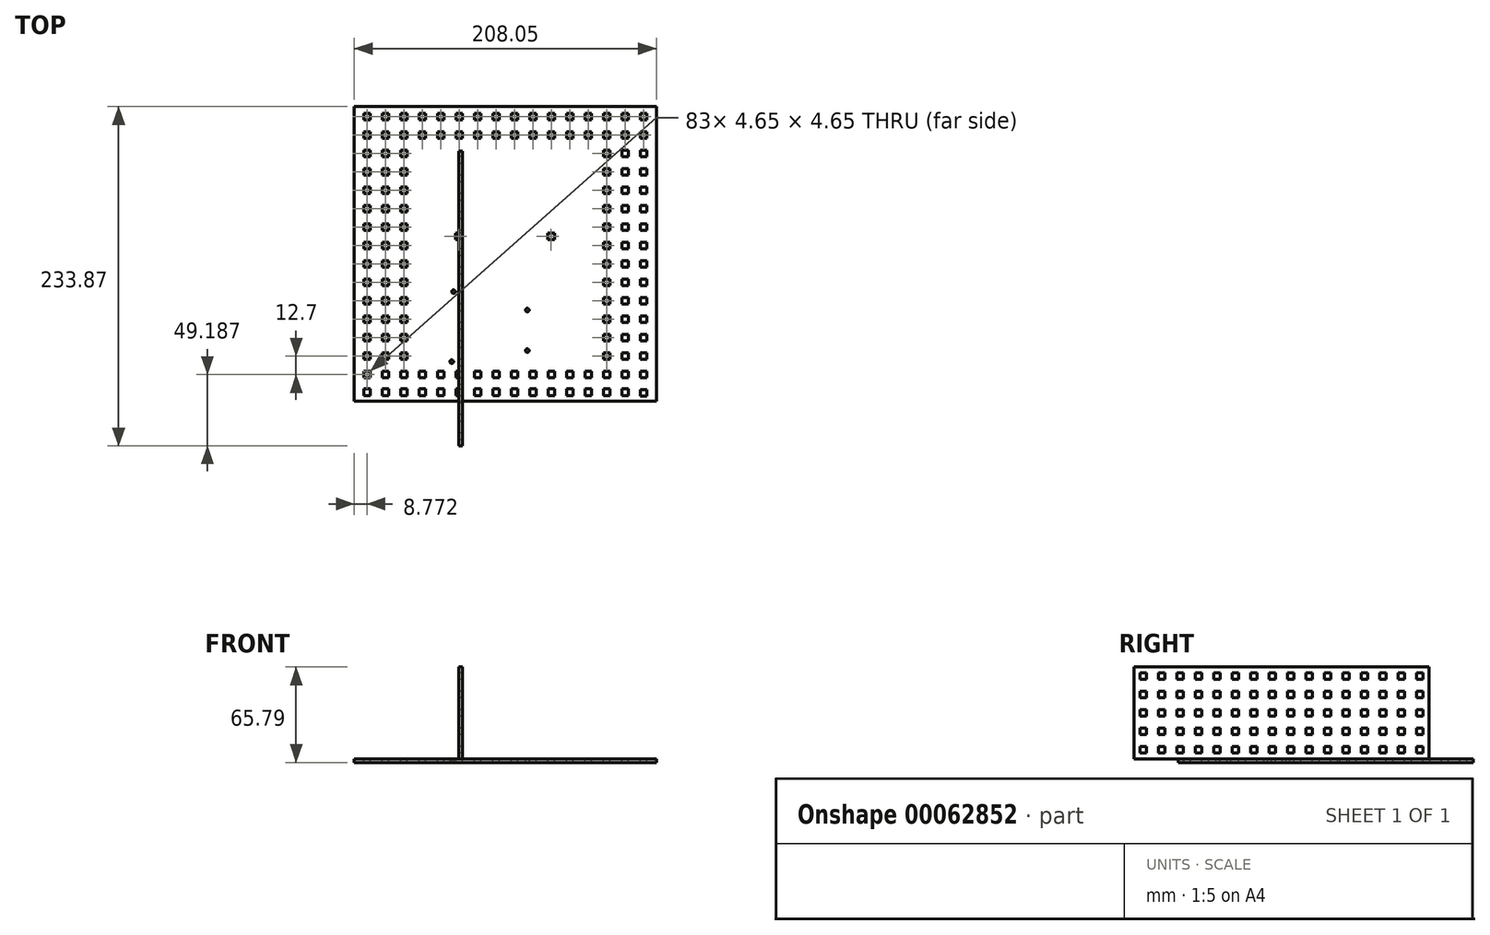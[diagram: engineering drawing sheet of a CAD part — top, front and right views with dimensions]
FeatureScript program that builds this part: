
annotation { "Feature Type Name" : "Feature", "Feature Type Description" : "" }
export const myFeature = defineFeature(function(context is Context, id is Id, definition is map)
    precondition{}
    {
        {
            var Q0;
            Q0=qCreatedBy(makeId("Top.planeOp"),FACE);
            var sketch = newSketch(context, id + "F0", { "sketchPlane" : qUnion([Q0])});
            skLineSegment(sketch, "E0.bottom", {"start": v(129.56, 111.67) * mm, "end": v(124.9, 111.67) * mm});
            skLineSegment(sketch, "E0.top", {"start": v(129.56, 107.05) * mm, "end": v(124.9, 107.05) * mm});
            skLineSegment(sketch, "E0.left", {"start": v(129.56, 111.67) * mm, "end": v(129.56, 107.05) * mm});
            skLineSegment(sketch, "E0.right", {"start": v(124.9, 111.67) * mm, "end": v(124.9, 107.05) * mm});
            skLineSegment(sketch, "E1.0.1.0", {"start": v(129.56, 94.35) * mm, "end": v(124.93, 94.35) * mm});
            skLineSegment(sketch, "E1.0.1.1", {"start": v(129.56, 98.97) * mm, "end": v(129.56, 94.35) * mm});
            skLineSegment(sketch, "E1.0.1.2", {"start": v(124.93, 98.97) * mm, "end": v(124.93, 94.35) * mm});
            skLineSegment(sketch, "E1.0.1.3", {"start": v(129.56, 98.97) * mm, "end": v(124.93, 98.97) * mm});
            skLineSegment(sketch, "E1.0.2.0", {"start": v(129.56, 81.65) * mm, "end": v(124.93, 81.65) * mm});
            skLineSegment(sketch, "E1.0.2.1", {"start": v(129.56, 86.27) * mm, "end": v(129.56, 81.65) * mm});
            skLineSegment(sketch, "E1.0.2.2", {"start": v(124.93, 86.27) * mm, "end": v(124.93, 81.65) * mm});
            skLineSegment(sketch, "E1.0.2.3", {"start": v(129.56, 86.27) * mm, "end": v(124.93, 86.27) * mm});
            skLineSegment(sketch, "E1.0.3.0", {"start": v(129.56, 68.95) * mm, "end": v(124.93, 68.95) * mm});
            skLineSegment(sketch, "E1.0.3.1", {"start": v(129.56, 73.57) * mm, "end": v(129.56, 68.95) * mm});
            skLineSegment(sketch, "E1.0.3.2", {"start": v(124.93, 73.57) * mm, "end": v(124.93, 68.95) * mm});
            skLineSegment(sketch, "E1.0.3.3", {"start": v(129.56, 73.57) * mm, "end": v(124.93, 73.57) * mm});
            skLineSegment(sketch, "E1.0.4.0", {"start": v(129.56, 56.25) * mm, "end": v(124.93, 56.25) * mm});
            skLineSegment(sketch, "E1.0.4.1", {"start": v(129.56, 60.87) * mm, "end": v(129.56, 56.25) * mm});
            skLineSegment(sketch, "E1.0.4.2", {"start": v(124.93, 60.87) * mm, "end": v(124.93, 56.25) * mm});
            skLineSegment(sketch, "E1.0.4.3", {"start": v(129.56, 60.87) * mm, "end": v(124.93, 60.87) * mm});
            skLineSegment(sketch, "E1.0.5.0", {"start": v(129.56, 43.55) * mm, "end": v(124.93, 43.55) * mm});
            skLineSegment(sketch, "E1.0.5.1", {"start": v(129.56, 48.17) * mm, "end": v(129.56, 43.55) * mm});
            skLineSegment(sketch, "E1.0.5.2", {"start": v(124.93, 48.17) * mm, "end": v(124.93, 43.55) * mm});
            skLineSegment(sketch, "E1.0.5.3", {"start": v(129.56, 48.17) * mm, "end": v(124.93, 48.17) * mm});
            skLineSegment(sketch, "E1.0.6.0", {"start": v(129.56, 30.85) * mm, "end": v(124.93, 30.85) * mm});
            skLineSegment(sketch, "E1.0.6.1", {"start": v(129.56, 35.47) * mm, "end": v(129.56, 30.85) * mm});
            skLineSegment(sketch, "E1.0.6.2", {"start": v(124.93, 35.47) * mm, "end": v(124.93, 30.85) * mm});
            skLineSegment(sketch, "E1.0.6.3", {"start": v(129.56, 35.47) * mm, "end": v(124.93, 35.47) * mm});
            skLineSegment(sketch, "E1.0.7.0", {"start": v(129.56, 18.15) * mm, "end": v(124.93, 18.15) * mm});
            skLineSegment(sketch, "E1.0.7.1", {"start": v(129.56, 22.77) * mm, "end": v(129.56, 18.15) * mm});
            skLineSegment(sketch, "E1.0.7.2", {"start": v(124.93, 22.77) * mm, "end": v(124.93, 18.15) * mm});
            skLineSegment(sketch, "E1.0.7.3", {"start": v(129.56, 22.77) * mm, "end": v(124.93, 22.77) * mm});
            skLineSegment(sketch, "E1.0.8.0", {"start": v(129.56, 5.45) * mm, "end": v(124.93, 5.45) * mm});
            skLineSegment(sketch, "E1.0.8.1", {"start": v(129.56, 10.07) * mm, "end": v(129.56, 5.45) * mm});
            skLineSegment(sketch, "E1.0.8.2", {"start": v(124.93, 10.07) * mm, "end": v(124.93, 5.45) * mm});
            skLineSegment(sketch, "E1.0.8.3", {"start": v(129.56, 10.07) * mm, "end": v(124.93, 10.07) * mm});
            skLineSegment(sketch, "E1.0.9.0", {"start": v(129.56, -7.25) * mm, "end": v(124.93, -7.25) * mm});
            skLineSegment(sketch, "E1.0.9.1", {"start": v(129.56, -2.63) * mm, "end": v(129.56, -7.25) * mm});
            skLineSegment(sketch, "E1.0.9.2", {"start": v(124.93, -2.63) * mm, "end": v(124.93, -7.25) * mm});
            skLineSegment(sketch, "E1.0.9.3", {"start": v(129.56, -2.63) * mm, "end": v(124.93, -2.63) * mm});
            skLineSegment(sketch, "E1.0.10.0", {"start": v(129.56, -19.95) * mm, "end": v(124.93, -19.95) * mm});
            skLineSegment(sketch, "E1.0.10.1", {"start": v(129.56, -15.33) * mm, "end": v(129.56, -19.95) * mm});
            skLineSegment(sketch, "E1.0.10.2", {"start": v(124.93, -15.33) * mm, "end": v(124.93, -19.95) * mm});
            skLineSegment(sketch, "E1.0.10.3", {"start": v(129.56, -15.33) * mm, "end": v(124.93, -15.33) * mm});
            skLineSegment(sketch, "E2", {"start": v(-72.04, 141.63) * mm, "end": v(-72.04, -61.57) * mm});
            skLineSegment(sketch, "E3.0.0.12", {"start": v(-60.94, -40.73) * mm, "end": v(-60.94, -45.35) * mm});
            skLineSegment(sketch, "E3.3.0.12", {"start": v(-65.57, -45.35) * mm, "end": v(-60.94, -45.35) * mm});
            skLineSegment(sketch, "E3.6.0.12", {"start": v(-65.57, -40.73) * mm, "end": v(-65.57, -45.35) * mm});
            skLineSegment(sketch, "E3.9.0.12", {"start": v(-65.57, -40.73) * mm, "end": v(-60.94, -40.73) * mm});
            skLineSegment(sketch, "E3.0.0.13", {"start": v(-60.92, -52.9) * mm, "end": v(-60.92, -57.53) * mm});
            skLineSegment(sketch, "E3.3.0.13", {"start": v(-65.57, -57.53) * mm, "end": v(-60.92, -57.53) * mm});
            skLineSegment(sketch, "E3.6.0.13", {"start": v(-65.57, -52.9) * mm, "end": v(-65.57, -57.53) * mm});
            skLineSegment(sketch, "E3.9.0.13", {"start": v(-65.57, -52.9) * mm, "end": v(-60.92, -52.9) * mm});
            skLineSegment(sketch, "E4.0.0.11", {"start": v(129.56, -32.65) * mm, "end": v(124.93, -32.65) * mm});
            skLineSegment(sketch, "E4.3.0.11", {"start": v(129.56, -28.03) * mm, "end": v(129.56, -32.65) * mm});
            skLineSegment(sketch, "E4.6.0.11", {"start": v(124.93, -28.03) * mm, "end": v(124.93, -32.65) * mm});
            skLineSegment(sketch, "E4.9.0.11", {"start": v(129.56, -28.03) * mm, "end": v(124.93, -28.03) * mm});
            skLineSegment(sketch, "E4.0.0.12", {"start": v(129.56, -45.35) * mm, "end": v(124.93, -45.35) * mm});
            skLineSegment(sketch, "E4.3.0.12", {"start": v(129.56, -40.73) * mm, "end": v(129.56, -45.35) * mm});
            skLineSegment(sketch, "E4.6.0.12", {"start": v(124.93, -40.73) * mm, "end": v(124.93, -45.35) * mm});
            skLineSegment(sketch, "E4.9.0.12", {"start": v(129.56, -40.73) * mm, "end": v(124.93, -40.73) * mm});
            skLineSegment(sketch, "E4.0.0.13", {"start": v(129.56, -58.05) * mm, "end": v(124.93, -58.05) * mm});
            skLineSegment(sketch, "E4.3.0.13", {"start": v(129.56, -53.43) * mm, "end": v(129.56, -58.05) * mm});
            skLineSegment(sketch, "E4.6.0.13", {"start": v(124.93, -53.43) * mm, "end": v(124.93, -58.05) * mm});
            skLineSegment(sketch, "E4.9.0.13", {"start": v(129.56, -53.43) * mm, "end": v(124.93, -53.43) * mm});
            skCircle(sketch, "E5", {"center": v(-3.7, 14.1) * mm, "radius": 1.27 * mm});
            skCircle(sketch, "E6", {"center": v(47.1, 1.4) * mm, "radius": 1.27 * mm});
            skCircle(sketch, "E7", {"center": v(47.1, -26.53) * mm, "radius": 1.27 * mm});
            skCircle(sketch, "E8", {"center": v(-4.96, -34.15) * mm, "radius": 1.27 * mm});
            skLineSegment(sketch, "E9", {"start": v(-60.94, 137.07) * mm, "end": v(-60.94, 132.42) * mm});
            skLineSegment(sketch, "E10", {"start": v(-60.94, 132.42) * mm, "end": v(-65.6, 132.42) * mm});
            skLineSegment(sketch, "E11", {"start": v(124.9, 124.37) * mm, "end": v(129.56, 124.37) * mm});
            skLineSegment(sketch, "E12", {"start": v(129.56, 124.37) * mm, "end": v(129.56, 119.72) * mm});
            skLineSegment(sketch, "E13", {"start": v(124.9, 137.07) * mm, "end": v(129.56, 137.07) * mm});
            skLineSegment(sketch, "E14", {"start": v(129.56, 137.07) * mm, "end": v(129.56, 132.42) * mm});
            skLineSegment(sketch, "E15", {"start": v(129.56, 132.42) * mm, "end": v(124.9, 132.42) * mm});
            skLineSegment(sketch, "E16", {"start": v(129.56, 119.72) * mm, "end": v(124.9, 119.72) * mm});
            skLineSegment(sketch, "E17", {"start": v(124.9, 119.72) * mm, "end": v(124.9, 124.37) * mm});
            skLineSegment(sketch, "E18", {"start": v(124.9, 137.07) * mm, "end": v(124.9, 132.42) * mm});
            skLineSegment(sketch, "E19.rect.bottom", {"start": v(2.32, 49.89) * mm, "end": v(-2.32, 49.89) * mm});
            skLineSegment(sketch, "E19.rect.top", {"start": v(2.32, 54.53) * mm, "end": v(-2.32, 54.53) * mm});
            skLineSegment(sketch, "E19.rect.left", {"start": v(2.32, 49.89) * mm, "end": v(2.32, 54.53) * mm});
            skLineSegment(sketch, "E19.rect.right", {"start": v(-2.32, 49.89) * mm, "end": v(-2.32, 54.53) * mm});
            skPoint(sketch, "E19.rect.middle", {"position": v(0, 52.2) * mm});
            skLineSegment(sketch, "E20.rect.bottom", {"start": v(65.82, 49.89) * mm, "end": v(61.18, 49.89) * mm});
            skLineSegment(sketch, "E20.rect.top", {"start": v(65.82, 54.53) * mm, "end": v(61.18, 54.53) * mm});
            skLineSegment(sketch, "E20.rect.left", {"start": v(65.82, 49.89) * mm, "end": v(65.82, 54.53) * mm});
            skLineSegment(sketch, "E20.rect.right", {"start": v(61.18, 49.89) * mm, "end": v(61.18, 54.53) * mm});
            skPoint(sketch, "E20.rect.middle", {"position": v(63.5, 52.2) * mm});
            skLineSegment(sketch, "E21", {"start": v(-72.04, -61.57) * mm, "end": v(136, -61.57) * mm});
            skLineSegment(sketch, "E22", {"start": v(136, 141.63) * mm, "end": v(136, -61.57) * mm});
            skLineSegment(sketch, "E23", {"start": v(-72.04, 141.63) * mm, "end": v(136, 141.63) * mm});
            skLineSegment(sketch, "E24", {"start": v(-60.94, 137.07) * mm, "end": v(-65.6, 137.07) * mm});
            skLineSegment(sketch, "E25", {"start": v(-65.6, 137.07) * mm, "end": v(-65.6, 132.42) * mm});
            skLineSegment(sketch, "E26.1.0.0", {"start": v(-48.24, 137.07) * mm, "end": v(-48.24, 132.42) * mm});
            skLineSegment(sketch, "E26.1.0.1", {"start": v(-48.24, 137.07) * mm, "end": v(-52.9, 137.07) * mm});
            skLineSegment(sketch, "E26.1.0.2", {"start": v(-52.9, 137.07) * mm, "end": v(-52.9, 132.42) * mm});
            skLineSegment(sketch, "E26.1.0.3", {"start": v(-48.24, 132.42) * mm, "end": v(-52.9, 132.42) * mm});
            skLineSegment(sketch, "E26.2.0.0", {"start": v(-35.54, 137.07) * mm, "end": v(-35.54, 132.42) * mm});
            skLineSegment(sketch, "E26.2.0.1", {"start": v(-35.54, 137.07) * mm, "end": v(-40.2, 137.07) * mm});
            skLineSegment(sketch, "E26.2.0.2", {"start": v(-40.2, 137.07) * mm, "end": v(-40.2, 132.42) * mm});
            skLineSegment(sketch, "E26.2.0.3", {"start": v(-35.54, 132.42) * mm, "end": v(-40.2, 132.42) * mm});
            skLineSegment(sketch, "E26.3.0.0", {"start": v(-22.84, 137.07) * mm, "end": v(-22.84, 132.42) * mm});
            skLineSegment(sketch, "E26.3.0.1", {"start": v(-22.84, 137.07) * mm, "end": v(-27.5, 137.07) * mm});
            skLineSegment(sketch, "E26.3.0.2", {"start": v(-27.5, 137.07) * mm, "end": v(-27.5, 132.42) * mm});
            skLineSegment(sketch, "E26.3.0.3", {"start": v(-22.84, 132.42) * mm, "end": v(-27.5, 132.42) * mm});
            skLineSegment(sketch, "E26.4.0.0", {"start": v(-10.14, 137.07) * mm, "end": v(-10.14, 132.42) * mm});
            skLineSegment(sketch, "E26.4.0.1", {"start": v(-10.14, 137.07) * mm, "end": v(-14.8, 137.07) * mm});
            skLineSegment(sketch, "E26.4.0.2", {"start": v(-14.8, 137.07) * mm, "end": v(-14.8, 132.42) * mm});
            skLineSegment(sketch, "E26.4.0.3", {"start": v(-10.14, 132.42) * mm, "end": v(-14.8, 132.42) * mm});
            skLineSegment(sketch, "E26.5.0.0", {"start": v(2.56, 137.07) * mm, "end": v(2.56, 132.42) * mm});
            skLineSegment(sketch, "E26.5.0.1", {"start": v(2.56, 137.07) * mm, "end": v(-2.1, 137.07) * mm});
            skLineSegment(sketch, "E26.5.0.2", {"start": v(-2.1, 137.07) * mm, "end": v(-2.1, 132.42) * mm});
            skLineSegment(sketch, "E26.5.0.3", {"start": v(2.56, 132.42) * mm, "end": v(-2.1, 132.42) * mm});
            skLineSegment(sketch, "E26.6.0.0", {"start": v(15.26, 137.07) * mm, "end": v(15.26, 132.42) * mm});
            skLineSegment(sketch, "E26.6.0.1", {"start": v(15.26, 137.07) * mm, "end": v(10.6, 137.07) * mm});
            skLineSegment(sketch, "E26.6.0.2", {"start": v(10.6, 137.07) * mm, "end": v(10.6, 132.42) * mm});
            skLineSegment(sketch, "E26.6.0.3", {"start": v(15.26, 132.42) * mm, "end": v(10.6, 132.42) * mm});
            skLineSegment(sketch, "E26.7.0.0", {"start": v(27.96, 137.07) * mm, "end": v(27.96, 132.42) * mm});
            skLineSegment(sketch, "E26.7.0.1", {"start": v(27.96, 137.07) * mm, "end": v(23.3, 137.07) * mm});
            skLineSegment(sketch, "E26.7.0.2", {"start": v(23.3, 137.07) * mm, "end": v(23.3, 132.42) * mm});
            skLineSegment(sketch, "E26.7.0.3", {"start": v(27.96, 132.42) * mm, "end": v(23.3, 132.42) * mm});
            skLineSegment(sketch, "E26.8.0.0", {"start": v(40.66, 137.07) * mm, "end": v(40.66, 132.42) * mm});
            skLineSegment(sketch, "E26.8.0.1", {"start": v(40.66, 137.07) * mm, "end": v(36, 137.07) * mm});
            skLineSegment(sketch, "E26.8.0.2", {"start": v(36, 137.07) * mm, "end": v(36, 132.42) * mm});
            skLineSegment(sketch, "E26.8.0.3", {"start": v(40.66, 132.42) * mm, "end": v(36, 132.42) * mm});
            skLineSegment(sketch, "E26.9.0.0", {"start": v(53.36, 137.07) * mm, "end": v(53.36, 132.42) * mm});
            skLineSegment(sketch, "E26.9.0.1", {"start": v(53.36, 137.07) * mm, "end": v(48.7, 137.07) * mm});
            skLineSegment(sketch, "E26.9.0.2", {"start": v(48.7, 137.07) * mm, "end": v(48.7, 132.42) * mm});
            skLineSegment(sketch, "E26.9.0.3", {"start": v(53.36, 132.42) * mm, "end": v(48.7, 132.42) * mm});
            skLineSegment(sketch, "E26.10.0.0", {"start": v(66.06, 137.07) * mm, "end": v(66.06, 132.42) * mm});
            skLineSegment(sketch, "E26.10.0.1", {"start": v(66.06, 137.07) * mm, "end": v(61.4, 137.07) * mm});
            skLineSegment(sketch, "E26.10.0.2", {"start": v(61.4, 137.07) * mm, "end": v(61.4, 132.42) * mm});
            skLineSegment(sketch, "E26.10.0.3", {"start": v(66.06, 132.42) * mm, "end": v(61.4, 132.42) * mm});
            skLineSegment(sketch, "E26.11.0.0", {"start": v(78.76, 137.07) * mm, "end": v(78.76, 132.42) * mm});
            skLineSegment(sketch, "E26.11.0.1", {"start": v(78.76, 137.07) * mm, "end": v(74.1, 137.07) * mm});
            skLineSegment(sketch, "E26.11.0.2", {"start": v(74.1, 137.07) * mm, "end": v(74.1, 132.42) * mm});
            skLineSegment(sketch, "E26.11.0.3", {"start": v(78.76, 132.42) * mm, "end": v(74.1, 132.42) * mm});
            skLineSegment(sketch, "E26.12.0.0", {"start": v(91.46, 137.07) * mm, "end": v(91.46, 132.42) * mm});
            skLineSegment(sketch, "E26.12.0.1", {"start": v(91.46, 137.07) * mm, "end": v(86.8, 137.07) * mm});
            skLineSegment(sketch, "E26.12.0.2", {"start": v(86.8, 137.07) * mm, "end": v(86.8, 132.42) * mm});
            skLineSegment(sketch, "E26.12.0.3", {"start": v(91.46, 132.42) * mm, "end": v(86.8, 132.42) * mm});
            skLineSegment(sketch, "E26.13.0.0", {"start": v(104.16, 137.07) * mm, "end": v(104.16, 132.42) * mm});
            skLineSegment(sketch, "E26.13.0.1", {"start": v(104.16, 137.07) * mm, "end": v(99.5, 137.07) * mm});
            skLineSegment(sketch, "E26.13.0.2", {"start": v(99.5, 137.07) * mm, "end": v(99.5, 132.42) * mm});
            skLineSegment(sketch, "E26.13.0.3", {"start": v(104.16, 132.42) * mm, "end": v(99.5, 132.42) * mm});
            skLineSegment(sketch, "E26.14.0.0", {"start": v(116.86, 137.07) * mm, "end": v(116.86, 132.42) * mm});
            skLineSegment(sketch, "E26.14.0.1", {"start": v(116.86, 137.07) * mm, "end": v(112.2, 137.07) * mm});
            skLineSegment(sketch, "E26.14.0.2", {"start": v(112.2, 137.07) * mm, "end": v(112.2, 132.42) * mm});
            skLineSegment(sketch, "E26.14.0.3", {"start": v(116.86, 132.42) * mm, "end": v(112.2, 132.42) * mm});
            skLineSegment(sketch, "E26.direction1", {"start": v(-60.94, 132.42) * mm, "end": v(-48.24, 132.42) * mm, "construction": true});
            skLineSegment(sketch, "E27", {"start": v(-65.6, 137.07) * mm, "end": v(-72.04, 137.07) * mm});
            skLineSegment(sketch, "E28", {"start": v(-65.6, 124.26) * mm, "end": v(-72.04, 124.26) * mm});
            skLineSegment(sketch, "E29", {"start": v(-65.57, -40.73) * mm, "end": v(-72.04, -40.73) * mm});
            skLineSegment(sketch, "E30", {"start": v(129.56, 124.37) * mm, "end": v(136, 124.37) * mm});
            skLineSegment(sketch, "E31", {"start": v(129.56, 111.67) * mm, "end": v(136, 111.67) * mm});
            skLineSegment(sketch, "E32", {"start": v(129.56, 98.97) * mm, "end": v(136, 98.97) * mm});
            skLineSegment(sketch, "E33", {"start": v(129.56, 86.27) * mm, "end": v(136, 86.27) * mm});
            skLineSegment(sketch, "E34", {"start": v(129.56, 73.57) * mm, "end": v(136, 73.57) * mm});
            skLineSegment(sketch, "E35", {"start": v(129.56, 60.87) * mm, "end": v(136, 60.87) * mm});
            skLineSegment(sketch, "E36", {"start": v(129.56, 48.17) * mm, "end": v(136, 48.17) * mm});
            skLineSegment(sketch, "E37", {"start": v(129.56, 35.47) * mm, "end": v(136, 35.47) * mm});
            skLineSegment(sketch, "E38", {"start": v(129.56, 22.77) * mm, "end": v(136, 22.77) * mm});
            skLineSegment(sketch, "E39", {"start": v(129.56, 10.07) * mm, "end": v(136, 10.07) * mm});
            skLineSegment(sketch, "E40", {"start": v(129.56, -2.63) * mm, "end": v(136, -2.63) * mm});
            skLineSegment(sketch, "E41", {"start": v(129.56, -15.33) * mm, "end": v(136, -15.33) * mm});
            skLineSegment(sketch, "E42", {"start": v(129.56, -28.03) * mm, "end": v(136, -28.03) * mm});
            skLineSegment(sketch, "E43", {"start": v(129.56, -40.73) * mm, "end": v(136, -40.73) * mm});
            skLineSegment(sketch, "E44", {"start": v(129.56, -53.43) * mm, "end": v(136, -53.43) * mm});
            skLineSegment(sketch, "E45.1.0.0", {"start": v(-48.22, -52.9) * mm, "end": v(-48.22, -57.53) * mm});
            skLineSegment(sketch, "E45.1.0.1", {"start": v(-52.87, -52.9) * mm, "end": v(-48.22, -52.9) * mm});
            skLineSegment(sketch, "E45.1.0.2", {"start": v(-52.87, -52.9) * mm, "end": v(-52.87, -57.53) * mm});
            skLineSegment(sketch, "E45.1.0.3", {"start": v(-52.87, -57.53) * mm, "end": v(-48.22, -57.53) * mm});
            skLineSegment(sketch, "E45.2.0.0", {"start": v(-35.52, -52.9) * mm, "end": v(-35.52, -57.53) * mm});
            skLineSegment(sketch, "E45.2.0.1", {"start": v(-40.17, -52.9) * mm, "end": v(-35.52, -52.9) * mm});
            skLineSegment(sketch, "E45.2.0.2", {"start": v(-40.17, -52.9) * mm, "end": v(-40.17, -57.53) * mm});
            skLineSegment(sketch, "E45.2.0.3", {"start": v(-40.17, -57.53) * mm, "end": v(-35.52, -57.53) * mm});
            skLineSegment(sketch, "E45.3.0.0", {"start": v(-22.82, -52.9) * mm, "end": v(-22.82, -57.53) * mm});
            skLineSegment(sketch, "E45.3.0.1", {"start": v(-27.47, -52.9) * mm, "end": v(-22.82, -52.9) * mm});
            skLineSegment(sketch, "E45.3.0.2", {"start": v(-27.47, -52.9) * mm, "end": v(-27.47, -57.53) * mm});
            skLineSegment(sketch, "E45.3.0.3", {"start": v(-27.47, -57.53) * mm, "end": v(-22.82, -57.53) * mm});
            skLineSegment(sketch, "E45.4.0.0", {"start": v(-10.12, -52.9) * mm, "end": v(-10.12, -57.53) * mm});
            skLineSegment(sketch, "E45.4.0.1", {"start": v(-14.77, -52.9) * mm, "end": v(-10.12, -52.9) * mm});
            skLineSegment(sketch, "E45.4.0.2", {"start": v(-14.77, -52.9) * mm, "end": v(-14.77, -57.53) * mm});
            skLineSegment(sketch, "E45.4.0.3", {"start": v(-14.77, -57.53) * mm, "end": v(-10.12, -57.53) * mm});
            skLineSegment(sketch, "E45.5.0.0", {"start": v(2.58, -52.9) * mm, "end": v(2.58, -57.53) * mm});
            skLineSegment(sketch, "E45.5.0.1", {"start": v(-2.07, -52.9) * mm, "end": v(2.58, -52.9) * mm});
            skLineSegment(sketch, "E45.5.0.2", {"start": v(-2.07, -52.9) * mm, "end": v(-2.07, -57.53) * mm});
            skLineSegment(sketch, "E45.5.0.3", {"start": v(-2.07, -57.53) * mm, "end": v(2.58, -57.53) * mm});
            skLineSegment(sketch, "E45.6.0.0", {"start": v(15.28, -52.9) * mm, "end": v(15.28, -57.53) * mm});
            skLineSegment(sketch, "E45.6.0.1", {"start": v(10.63, -52.9) * mm, "end": v(15.28, -52.9) * mm});
            skLineSegment(sketch, "E45.6.0.2", {"start": v(10.63, -52.9) * mm, "end": v(10.63, -57.53) * mm});
            skLineSegment(sketch, "E45.6.0.3", {"start": v(10.63, -57.53) * mm, "end": v(15.28, -57.53) * mm});
            skLineSegment(sketch, "E45.7.0.0", {"start": v(27.98, -52.9) * mm, "end": v(27.98, -57.53) * mm});
            skLineSegment(sketch, "E45.7.0.1", {"start": v(23.33, -52.9) * mm, "end": v(27.98, -52.9) * mm});
            skLineSegment(sketch, "E45.7.0.2", {"start": v(23.33, -52.9) * mm, "end": v(23.33, -57.53) * mm});
            skLineSegment(sketch, "E45.7.0.3", {"start": v(23.33, -57.53) * mm, "end": v(27.98, -57.53) * mm});
            skLineSegment(sketch, "E45.8.0.0", {"start": v(40.68, -52.9) * mm, "end": v(40.68, -57.53) * mm});
            skLineSegment(sketch, "E45.8.0.1", {"start": v(36.03, -52.9) * mm, "end": v(40.68, -52.9) * mm});
            skLineSegment(sketch, "E45.8.0.2", {"start": v(36.03, -52.9) * mm, "end": v(36.03, -57.53) * mm});
            skLineSegment(sketch, "E45.8.0.3", {"start": v(36.03, -57.53) * mm, "end": v(40.68, -57.53) * mm});
            skLineSegment(sketch, "E45.9.0.0", {"start": v(53.38, -52.9) * mm, "end": v(53.38, -57.53) * mm});
            skLineSegment(sketch, "E45.9.0.1", {"start": v(48.73, -52.9) * mm, "end": v(53.38, -52.9) * mm});
            skLineSegment(sketch, "E45.9.0.2", {"start": v(48.73, -52.9) * mm, "end": v(48.73, -57.53) * mm});
            skLineSegment(sketch, "E45.9.0.3", {"start": v(48.73, -57.53) * mm, "end": v(53.38, -57.53) * mm});
            skLineSegment(sketch, "E45.10.0.0", {"start": v(66.08, -52.9) * mm, "end": v(66.08, -57.53) * mm});
            skLineSegment(sketch, "E45.10.0.1", {"start": v(61.43, -52.9) * mm, "end": v(66.08, -52.9) * mm});
            skLineSegment(sketch, "E45.10.0.2", {"start": v(61.43, -52.9) * mm, "end": v(61.43, -57.53) * mm});
            skLineSegment(sketch, "E45.10.0.3", {"start": v(61.43, -57.53) * mm, "end": v(66.08, -57.53) * mm});
            skLineSegment(sketch, "E45.11.0.0", {"start": v(78.78, -52.9) * mm, "end": v(78.78, -57.53) * mm});
            skLineSegment(sketch, "E45.11.0.1", {"start": v(74.13, -52.9) * mm, "end": v(78.78, -52.9) * mm});
            skLineSegment(sketch, "E45.11.0.2", {"start": v(74.13, -52.9) * mm, "end": v(74.13, -57.53) * mm});
            skLineSegment(sketch, "E45.11.0.3", {"start": v(74.13, -57.53) * mm, "end": v(78.78, -57.53) * mm});
            skLineSegment(sketch, "E45.12.0.0", {"start": v(91.48, -52.9) * mm, "end": v(91.48, -57.53) * mm});
            skLineSegment(sketch, "E45.12.0.1", {"start": v(86.83, -52.9) * mm, "end": v(91.48, -52.9) * mm});
            skLineSegment(sketch, "E45.12.0.2", {"start": v(86.83, -52.9) * mm, "end": v(86.83, -57.53) * mm});
            skLineSegment(sketch, "E45.12.0.3", {"start": v(86.83, -57.53) * mm, "end": v(91.48, -57.53) * mm});
            skLineSegment(sketch, "E45.13.0.0", {"start": v(104.18, -52.9) * mm, "end": v(104.18, -57.53) * mm});
            skLineSegment(sketch, "E45.13.0.1", {"start": v(99.53, -52.9) * mm, "end": v(104.18, -52.9) * mm});
            skLineSegment(sketch, "E45.13.0.2", {"start": v(99.53, -52.9) * mm, "end": v(99.53, -57.53) * mm});
            skLineSegment(sketch, "E45.13.0.3", {"start": v(99.53, -57.53) * mm, "end": v(104.18, -57.53) * mm});
            skLineSegment(sketch, "E45.14.0.0", {"start": v(116.88, -52.9) * mm, "end": v(116.88, -57.53) * mm});
            skLineSegment(sketch, "E45.14.0.1", {"start": v(112.23, -52.9) * mm, "end": v(116.88, -52.9) * mm});
            skLineSegment(sketch, "E45.14.0.2", {"start": v(112.23, -52.9) * mm, "end": v(112.23, -57.53) * mm});
            skLineSegment(sketch, "E45.14.0.3", {"start": v(112.23, -57.53) * mm, "end": v(116.88, -57.53) * mm});
            skLineSegment(sketch, "E45.direction1", {"start": v(-60.92, -57.53) * mm, "end": v(-48.22, -57.53) * mm, "construction": true});
            skLineSegment(sketch, "E46.1.0.0", {"start": v(-48.24, -40.73) * mm, "end": v(-48.24, -45.35) * mm});
            skLineSegment(sketch, "E46.1.0.1", {"start": v(-52.87, -40.73) * mm, "end": v(-48.24, -40.73) * mm});
            skLineSegment(sketch, "E46.1.0.2", {"start": v(-52.87, -40.73) * mm, "end": v(-52.87, -45.35) * mm});
            skLineSegment(sketch, "E46.1.0.3", {"start": v(-52.87, -45.35) * mm, "end": v(-48.24, -45.35) * mm});
            skLineSegment(sketch, "E46.2.0.0", {"start": v(-35.54, -40.73) * mm, "end": v(-35.54, -45.35) * mm});
            skLineSegment(sketch, "E46.2.0.1", {"start": v(-40.17, -40.73) * mm, "end": v(-35.54, -40.73) * mm});
            skLineSegment(sketch, "E46.2.0.2", {"start": v(-40.17, -40.73) * mm, "end": v(-40.17, -45.35) * mm});
            skLineSegment(sketch, "E46.2.0.3", {"start": v(-40.17, -45.35) * mm, "end": v(-35.54, -45.35) * mm});
            skLineSegment(sketch, "E46.3.0.0", {"start": v(-22.84, -40.73) * mm, "end": v(-22.84, -45.35) * mm});
            skLineSegment(sketch, "E46.3.0.1", {"start": v(-27.47, -40.73) * mm, "end": v(-22.84, -40.73) * mm});
            skLineSegment(sketch, "E46.3.0.2", {"start": v(-27.47, -40.73) * mm, "end": v(-27.47, -45.35) * mm});
            skLineSegment(sketch, "E46.3.0.3", {"start": v(-27.47, -45.35) * mm, "end": v(-22.84, -45.35) * mm});
            skLineSegment(sketch, "E46.4.0.0", {"start": v(-10.14, -40.73) * mm, "end": v(-10.14, -45.35) * mm});
            skLineSegment(sketch, "E46.4.0.1", {"start": v(-14.77, -40.73) * mm, "end": v(-10.14, -40.73) * mm});
            skLineSegment(sketch, "E46.4.0.2", {"start": v(-14.77, -40.73) * mm, "end": v(-14.77, -45.35) * mm});
            skLineSegment(sketch, "E46.4.0.3", {"start": v(-14.77, -45.35) * mm, "end": v(-10.14, -45.35) * mm});
            skLineSegment(sketch, "E46.5.0.0", {"start": v(2.56, -40.73) * mm, "end": v(2.56, -45.35) * mm});
            skLineSegment(sketch, "E46.5.0.1", {"start": v(-2.07, -40.73) * mm, "end": v(2.56, -40.73) * mm});
            skLineSegment(sketch, "E46.5.0.2", {"start": v(-2.07, -40.73) * mm, "end": v(-2.07, -45.35) * mm});
            skLineSegment(sketch, "E46.5.0.3", {"start": v(-2.07, -45.35) * mm, "end": v(2.56, -45.35) * mm});
            skLineSegment(sketch, "E46.6.0.0", {"start": v(15.26, -40.73) * mm, "end": v(15.26, -45.35) * mm});
            skLineSegment(sketch, "E46.6.0.1", {"start": v(10.63, -40.73) * mm, "end": v(15.26, -40.73) * mm});
            skLineSegment(sketch, "E46.6.0.2", {"start": v(10.63, -40.73) * mm, "end": v(10.63, -45.35) * mm});
            skLineSegment(sketch, "E46.6.0.3", {"start": v(10.63, -45.35) * mm, "end": v(15.26, -45.35) * mm});
            skLineSegment(sketch, "E46.7.0.0", {"start": v(27.96, -40.73) * mm, "end": v(27.96, -45.35) * mm});
            skLineSegment(sketch, "E46.7.0.1", {"start": v(23.33, -40.73) * mm, "end": v(27.96, -40.73) * mm});
            skLineSegment(sketch, "E46.7.0.2", {"start": v(23.33, -40.73) * mm, "end": v(23.33, -45.35) * mm});
            skLineSegment(sketch, "E46.7.0.3", {"start": v(23.33, -45.35) * mm, "end": v(27.96, -45.35) * mm});
            skLineSegment(sketch, "E46.8.0.0", {"start": v(40.66, -40.73) * mm, "end": v(40.66, -45.35) * mm});
            skLineSegment(sketch, "E46.8.0.1", {"start": v(36.03, -40.73) * mm, "end": v(40.66, -40.73) * mm});
            skLineSegment(sketch, "E46.8.0.2", {"start": v(36.03, -40.73) * mm, "end": v(36.03, -45.35) * mm});
            skLineSegment(sketch, "E46.8.0.3", {"start": v(36.03, -45.35) * mm, "end": v(40.66, -45.35) * mm});
            skLineSegment(sketch, "E46.9.0.0", {"start": v(53.36, -40.73) * mm, "end": v(53.36, -45.35) * mm});
            skLineSegment(sketch, "E46.9.0.1", {"start": v(48.73, -40.73) * mm, "end": v(53.36, -40.73) * mm});
            skLineSegment(sketch, "E46.9.0.2", {"start": v(48.73, -40.73) * mm, "end": v(48.73, -45.35) * mm});
            skLineSegment(sketch, "E46.9.0.3", {"start": v(48.73, -45.35) * mm, "end": v(53.36, -45.35) * mm});
            skLineSegment(sketch, "E46.10.0.0", {"start": v(66.06, -40.73) * mm, "end": v(66.06, -45.35) * mm});
            skLineSegment(sketch, "E46.10.0.1", {"start": v(61.43, -40.73) * mm, "end": v(66.06, -40.73) * mm});
            skLineSegment(sketch, "E46.10.0.2", {"start": v(61.43, -40.73) * mm, "end": v(61.43, -45.35) * mm});
            skLineSegment(sketch, "E46.10.0.3", {"start": v(61.43, -45.35) * mm, "end": v(66.06, -45.35) * mm});
            skLineSegment(sketch, "E46.11.0.0", {"start": v(78.76, -40.73) * mm, "end": v(78.76, -45.35) * mm});
            skLineSegment(sketch, "E46.11.0.1", {"start": v(74.13, -40.73) * mm, "end": v(78.76, -40.73) * mm});
            skLineSegment(sketch, "E46.11.0.2", {"start": v(74.13, -40.73) * mm, "end": v(74.13, -45.35) * mm});
            skLineSegment(sketch, "E46.11.0.3", {"start": v(74.13, -45.35) * mm, "end": v(78.76, -45.35) * mm});
            skLineSegment(sketch, "E46.12.0.0", {"start": v(91.46, -40.73) * mm, "end": v(91.46, -45.35) * mm});
            skLineSegment(sketch, "E46.12.0.1", {"start": v(86.83, -40.73) * mm, "end": v(91.46, -40.73) * mm});
            skLineSegment(sketch, "E46.12.0.2", {"start": v(86.83, -40.73) * mm, "end": v(86.83, -45.35) * mm});
            skLineSegment(sketch, "E46.12.0.3", {"start": v(86.83, -45.35) * mm, "end": v(91.46, -45.35) * mm});
            skLineSegment(sketch, "E46.13.0.0", {"start": v(104.16, -40.73) * mm, "end": v(104.16, -45.35) * mm});
            skLineSegment(sketch, "E46.13.0.1", {"start": v(99.53, -40.73) * mm, "end": v(104.16, -40.73) * mm});
            skLineSegment(sketch, "E46.13.0.2", {"start": v(99.53, -40.73) * mm, "end": v(99.53, -45.35) * mm});
            skLineSegment(sketch, "E46.13.0.3", {"start": v(99.53, -45.35) * mm, "end": v(104.16, -45.35) * mm});
            skLineSegment(sketch, "E46.14.0.0", {"start": v(116.86, -40.73) * mm, "end": v(116.86, -45.35) * mm});
            skLineSegment(sketch, "E46.14.0.1", {"start": v(112.23, -40.73) * mm, "end": v(116.86, -40.73) * mm});
            skLineSegment(sketch, "E46.14.0.2", {"start": v(112.23, -40.73) * mm, "end": v(112.23, -45.35) * mm});
            skLineSegment(sketch, "E46.14.0.3", {"start": v(112.23, -45.35) * mm, "end": v(116.86, -45.35) * mm});
            skLineSegment(sketch, "E46.direction1", {"start": v(-60.94, -45.35) * mm, "end": v(-48.24, -45.35) * mm, "construction": true});
            skLineSegment(sketch, "E47.0.1.0", {"start": v(-60.94, 124.37) * mm, "end": v(-60.94, 119.72) * mm});
            skLineSegment(sketch, "E47.0.1.1", {"start": v(-60.94, 119.72) * mm, "end": v(-65.6, 119.72) * mm});
            skLineSegment(sketch, "E47.0.1.2", {"start": v(-65.6, 124.37) * mm, "end": v(-65.6, 119.72) * mm});
            skLineSegment(sketch, "E47.0.1.3", {"start": v(-60.94, 124.37) * mm, "end": v(-65.6, 124.37) * mm});
            skLineSegment(sketch, "E47.0.2.0", {"start": v(-60.94, 111.67) * mm, "end": v(-60.94, 107.02) * mm});
            skLineSegment(sketch, "E47.0.2.1", {"start": v(-60.94, 107.02) * mm, "end": v(-65.6, 107.02) * mm});
            skLineSegment(sketch, "E47.0.2.2", {"start": v(-65.6, 111.67) * mm, "end": v(-65.6, 107.02) * mm});
            skLineSegment(sketch, "E47.0.2.3", {"start": v(-60.94, 111.67) * mm, "end": v(-65.6, 111.67) * mm});
            skLineSegment(sketch, "E47.0.3.0", {"start": v(-60.94, 98.97) * mm, "end": v(-60.94, 94.32) * mm});
            skLineSegment(sketch, "E47.0.3.1", {"start": v(-60.94, 94.32) * mm, "end": v(-65.6, 94.32) * mm});
            skLineSegment(sketch, "E47.0.3.2", {"start": v(-65.6, 98.97) * mm, "end": v(-65.6, 94.32) * mm});
            skLineSegment(sketch, "E47.0.3.3", {"start": v(-60.94, 98.97) * mm, "end": v(-65.6, 98.97) * mm});
            skLineSegment(sketch, "E47.0.4.0", {"start": v(-60.94, 86.27) * mm, "end": v(-60.94, 81.62) * mm});
            skLineSegment(sketch, "E47.0.4.1", {"start": v(-60.94, 81.62) * mm, "end": v(-65.6, 81.62) * mm});
            skLineSegment(sketch, "E47.0.4.2", {"start": v(-65.6, 86.27) * mm, "end": v(-65.6, 81.62) * mm});
            skLineSegment(sketch, "E47.0.4.3", {"start": v(-60.94, 86.27) * mm, "end": v(-65.6, 86.27) * mm});
            skLineSegment(sketch, "E47.0.5.0", {"start": v(-60.94, 73.57) * mm, "end": v(-60.94, 68.92) * mm});
            skLineSegment(sketch, "E47.0.5.1", {"start": v(-60.94, 68.92) * mm, "end": v(-65.6, 68.92) * mm});
            skLineSegment(sketch, "E47.0.5.2", {"start": v(-65.6, 73.57) * mm, "end": v(-65.6, 68.92) * mm});
            skLineSegment(sketch, "E47.0.5.3", {"start": v(-60.94, 73.57) * mm, "end": v(-65.6, 73.57) * mm});
            skLineSegment(sketch, "E47.0.6.0", {"start": v(-60.94, 60.87) * mm, "end": v(-60.94, 56.22) * mm});
            skLineSegment(sketch, "E47.0.6.1", {"start": v(-60.94, 56.22) * mm, "end": v(-65.6, 56.22) * mm});
            skLineSegment(sketch, "E47.0.6.2", {"start": v(-65.6, 60.87) * mm, "end": v(-65.6, 56.22) * mm});
            skLineSegment(sketch, "E47.0.6.3", {"start": v(-60.94, 60.87) * mm, "end": v(-65.6, 60.87) * mm});
            skLineSegment(sketch, "E47.0.7.0", {"start": v(-60.94, 48.17) * mm, "end": v(-60.94, 43.52) * mm});
            skLineSegment(sketch, "E47.0.7.1", {"start": v(-60.94, 43.52) * mm, "end": v(-65.6, 43.52) * mm});
            skLineSegment(sketch, "E47.0.7.2", {"start": v(-65.6, 48.17) * mm, "end": v(-65.6, 43.52) * mm});
            skLineSegment(sketch, "E47.0.7.3", {"start": v(-60.94, 48.17) * mm, "end": v(-65.6, 48.17) * mm});
            skLineSegment(sketch, "E47.0.8.0", {"start": v(-60.94, 35.47) * mm, "end": v(-60.94, 30.82) * mm});
            skLineSegment(sketch, "E47.0.8.1", {"start": v(-60.94, 30.82) * mm, "end": v(-65.6, 30.82) * mm});
            skLineSegment(sketch, "E47.0.8.2", {"start": v(-65.6, 35.47) * mm, "end": v(-65.6, 30.82) * mm});
            skLineSegment(sketch, "E47.0.8.3", {"start": v(-60.94, 35.47) * mm, "end": v(-65.6, 35.47) * mm});
            skLineSegment(sketch, "E47.0.9.0", {"start": v(-60.94, 22.77) * mm, "end": v(-60.94, 18.12) * mm});
            skLineSegment(sketch, "E47.0.9.1", {"start": v(-60.94, 18.12) * mm, "end": v(-65.6, 18.12) * mm});
            skLineSegment(sketch, "E47.0.9.2", {"start": v(-65.6, 22.77) * mm, "end": v(-65.6, 18.12) * mm});
            skLineSegment(sketch, "E47.0.9.3", {"start": v(-60.94, 22.77) * mm, "end": v(-65.6, 22.77) * mm});
            skLineSegment(sketch, "E47.0.10.0", {"start": v(-60.94, 10.07) * mm, "end": v(-60.94, 5.42) * mm});
            skLineSegment(sketch, "E47.0.10.1", {"start": v(-60.94, 5.42) * mm, "end": v(-65.6, 5.42) * mm});
            skLineSegment(sketch, "E47.0.10.2", {"start": v(-65.6, 10.07) * mm, "end": v(-65.6, 5.42) * mm});
            skLineSegment(sketch, "E47.0.10.3", {"start": v(-60.94, 10.07) * mm, "end": v(-65.6, 10.07) * mm});
            skLineSegment(sketch, "E47.0.11.0", {"start": v(-60.94, -2.63) * mm, "end": v(-60.94, -7.28) * mm});
            skLineSegment(sketch, "E47.0.11.1", {"start": v(-60.94, -7.28) * mm, "end": v(-65.6, -7.28) * mm});
            skLineSegment(sketch, "E47.0.11.2", {"start": v(-65.6, -2.63) * mm, "end": v(-65.6, -7.28) * mm});
            skLineSegment(sketch, "E47.0.11.3", {"start": v(-60.94, -2.63) * mm, "end": v(-65.6, -2.63) * mm});
            skLineSegment(sketch, "E47.0.12.0", {"start": v(-60.94, -15.33) * mm, "end": v(-60.94, -19.98) * mm});
            skLineSegment(sketch, "E47.0.12.1", {"start": v(-60.94, -19.98) * mm, "end": v(-65.6, -19.98) * mm});
            skLineSegment(sketch, "E47.0.12.2", {"start": v(-65.6, -15.33) * mm, "end": v(-65.6, -19.98) * mm});
            skLineSegment(sketch, "E47.0.12.3", {"start": v(-60.94, -15.33) * mm, "end": v(-65.6, -15.33) * mm});
            skLineSegment(sketch, "E47.0.13.0", {"start": v(-60.94, -28.03) * mm, "end": v(-60.94, -32.68) * mm});
            skLineSegment(sketch, "E47.0.13.1", {"start": v(-60.94, -32.68) * mm, "end": v(-65.6, -32.68) * mm});
            skLineSegment(sketch, "E47.0.13.2", {"start": v(-65.6, -28.03) * mm, "end": v(-65.6, -32.68) * mm});
            skLineSegment(sketch, "E47.0.13.3", {"start": v(-60.94, -28.03) * mm, "end": v(-65.6, -28.03) * mm});
            skLineSegment(sketch, "E47.0.14.0", {"start": v(-60.94, -40.73) * mm, "end": v(-60.94, -45.38) * mm});
            skLineSegment(sketch, "E47.0.14.1", {"start": v(-60.94, -45.38) * mm, "end": v(-65.6, -45.38) * mm});
            skLineSegment(sketch, "E47.0.14.2", {"start": v(-65.6, -40.73) * mm, "end": v(-65.6, -45.38) * mm});
            skLineSegment(sketch, "E47.0.14.3", {"start": v(-60.94, -40.73) * mm, "end": v(-65.6, -40.73) * mm});
            skLineSegment(sketch, "E47.direction1", {"start": v(-60.94, 132.42) * mm, "end": v(-35.54, 132.42) * mm, "construction": true});
            skLineSegment(sketch, "E47.direction2", {"start": v(-60.94, 132.42) * mm, "end": v(-60.94, 119.72) * mm, "construction": true});
            skLineSegment(sketch, "E48.1.0.0", {"start": v(-48.24, 124.37) * mm, "end": v(-48.24, 119.72) * mm});
            skLineSegment(sketch, "E48.1.0.1", {"start": v(-48.24, 124.37) * mm, "end": v(-52.9, 124.37) * mm});
            skLineSegment(sketch, "E48.1.0.2", {"start": v(-52.9, 124.37) * mm, "end": v(-52.9, 119.72) * mm});
            skLineSegment(sketch, "E48.1.0.3", {"start": v(-48.24, 119.72) * mm, "end": v(-52.9, 119.72) * mm});
            skLineSegment(sketch, "E48.2.0.0", {"start": v(-35.54, 124.37) * mm, "end": v(-35.54, 119.72) * mm});
            skLineSegment(sketch, "E48.2.0.1", {"start": v(-35.54, 124.37) * mm, "end": v(-40.2, 124.37) * mm});
            skLineSegment(sketch, "E48.2.0.2", {"start": v(-40.2, 124.37) * mm, "end": v(-40.2, 119.72) * mm});
            skLineSegment(sketch, "E48.2.0.3", {"start": v(-35.54, 119.72) * mm, "end": v(-40.2, 119.72) * mm});
            skLineSegment(sketch, "E48.3.0.0", {"start": v(-22.84, 124.37) * mm, "end": v(-22.84, 119.72) * mm});
            skLineSegment(sketch, "E48.3.0.1", {"start": v(-22.84, 124.37) * mm, "end": v(-27.5, 124.37) * mm});
            skLineSegment(sketch, "E48.3.0.2", {"start": v(-27.5, 124.37) * mm, "end": v(-27.5, 119.72) * mm});
            skLineSegment(sketch, "E48.3.0.3", {"start": v(-22.84, 119.72) * mm, "end": v(-27.5, 119.72) * mm});
            skLineSegment(sketch, "E48.4.0.0", {"start": v(-10.14, 124.37) * mm, "end": v(-10.14, 119.72) * mm});
            skLineSegment(sketch, "E48.4.0.1", {"start": v(-10.14, 124.37) * mm, "end": v(-14.8, 124.37) * mm});
            skLineSegment(sketch, "E48.4.0.2", {"start": v(-14.8, 124.37) * mm, "end": v(-14.8, 119.72) * mm});
            skLineSegment(sketch, "E48.4.0.3", {"start": v(-10.14, 119.72) * mm, "end": v(-14.8, 119.72) * mm});
            skLineSegment(sketch, "E48.5.0.0", {"start": v(2.56, 124.37) * mm, "end": v(2.56, 119.72) * mm});
            skLineSegment(sketch, "E48.5.0.1", {"start": v(2.56, 124.37) * mm, "end": v(-2.1, 124.37) * mm});
            skLineSegment(sketch, "E48.5.0.2", {"start": v(-2.1, 124.37) * mm, "end": v(-2.1, 119.72) * mm});
            skLineSegment(sketch, "E48.5.0.3", {"start": v(2.56, 119.72) * mm, "end": v(-2.1, 119.72) * mm});
            skLineSegment(sketch, "E48.6.0.0", {"start": v(15.26, 124.37) * mm, "end": v(15.26, 119.72) * mm});
            skLineSegment(sketch, "E48.6.0.1", {"start": v(15.26, 124.37) * mm, "end": v(10.6, 124.37) * mm});
            skLineSegment(sketch, "E48.6.0.2", {"start": v(10.6, 124.37) * mm, "end": v(10.6, 119.72) * mm});
            skLineSegment(sketch, "E48.6.0.3", {"start": v(15.26, 119.72) * mm, "end": v(10.6, 119.72) * mm});
            skLineSegment(sketch, "E48.7.0.0", {"start": v(27.96, 124.37) * mm, "end": v(27.96, 119.72) * mm});
            skLineSegment(sketch, "E48.7.0.1", {"start": v(27.96, 124.37) * mm, "end": v(23.3, 124.37) * mm});
            skLineSegment(sketch, "E48.7.0.2", {"start": v(23.3, 124.37) * mm, "end": v(23.3, 119.72) * mm});
            skLineSegment(sketch, "E48.7.0.3", {"start": v(27.96, 119.72) * mm, "end": v(23.3, 119.72) * mm});
            skLineSegment(sketch, "E48.8.0.0", {"start": v(40.66, 124.37) * mm, "end": v(40.66, 119.72) * mm});
            skLineSegment(sketch, "E48.8.0.1", {"start": v(40.66, 124.37) * mm, "end": v(36, 124.37) * mm});
            skLineSegment(sketch, "E48.8.0.2", {"start": v(36, 124.37) * mm, "end": v(36, 119.72) * mm});
            skLineSegment(sketch, "E48.8.0.3", {"start": v(40.66, 119.72) * mm, "end": v(36, 119.72) * mm});
            skLineSegment(sketch, "E48.9.0.0", {"start": v(53.36, 124.37) * mm, "end": v(53.36, 119.72) * mm});
            skLineSegment(sketch, "E48.9.0.1", {"start": v(53.36, 124.37) * mm, "end": v(48.7, 124.37) * mm});
            skLineSegment(sketch, "E48.9.0.2", {"start": v(48.7, 124.37) * mm, "end": v(48.7, 119.72) * mm});
            skLineSegment(sketch, "E48.9.0.3", {"start": v(53.36, 119.72) * mm, "end": v(48.7, 119.72) * mm});
            skLineSegment(sketch, "E48.10.0.0", {"start": v(66.06, 124.37) * mm, "end": v(66.06, 119.72) * mm});
            skLineSegment(sketch, "E48.10.0.1", {"start": v(66.06, 124.37) * mm, "end": v(61.4, 124.37) * mm});
            skLineSegment(sketch, "E48.10.0.2", {"start": v(61.4, 124.37) * mm, "end": v(61.4, 119.72) * mm});
            skLineSegment(sketch, "E48.10.0.3", {"start": v(66.06, 119.72) * mm, "end": v(61.4, 119.72) * mm});
            skLineSegment(sketch, "E48.11.0.0", {"start": v(78.76, 124.37) * mm, "end": v(78.76, 119.72) * mm});
            skLineSegment(sketch, "E48.11.0.1", {"start": v(78.76, 124.37) * mm, "end": v(74.1, 124.37) * mm});
            skLineSegment(sketch, "E48.11.0.2", {"start": v(74.1, 124.37) * mm, "end": v(74.1, 119.72) * mm});
            skLineSegment(sketch, "E48.11.0.3", {"start": v(78.76, 119.72) * mm, "end": v(74.1, 119.72) * mm});
            skLineSegment(sketch, "E48.12.0.0", {"start": v(91.46, 124.37) * mm, "end": v(91.46, 119.72) * mm});
            skLineSegment(sketch, "E48.12.0.1", {"start": v(91.46, 124.37) * mm, "end": v(86.8, 124.37) * mm});
            skLineSegment(sketch, "E48.12.0.2", {"start": v(86.8, 124.37) * mm, "end": v(86.8, 119.72) * mm});
            skLineSegment(sketch, "E48.12.0.3", {"start": v(91.46, 119.72) * mm, "end": v(86.8, 119.72) * mm});
            skLineSegment(sketch, "E48.13.0.0", {"start": v(104.16, 124.37) * mm, "end": v(104.16, 119.72) * mm});
            skLineSegment(sketch, "E48.13.0.1", {"start": v(104.16, 124.37) * mm, "end": v(99.5, 124.37) * mm});
            skLineSegment(sketch, "E48.13.0.2", {"start": v(99.5, 124.37) * mm, "end": v(99.5, 119.72) * mm});
            skLineSegment(sketch, "E48.13.0.3", {"start": v(104.16, 119.72) * mm, "end": v(99.5, 119.72) * mm});
            skLineSegment(sketch, "E48.14.0.0", {"start": v(116.86, 124.37) * mm, "end": v(116.86, 119.72) * mm});
            skLineSegment(sketch, "E48.14.0.1", {"start": v(116.86, 124.37) * mm, "end": v(112.2, 124.37) * mm});
            skLineSegment(sketch, "E48.14.0.2", {"start": v(112.2, 124.37) * mm, "end": v(112.2, 119.72) * mm});
            skLineSegment(sketch, "E48.14.0.3", {"start": v(116.86, 119.72) * mm, "end": v(112.2, 119.72) * mm});
            skLineSegment(sketch, "E48.direction1", {"start": v(-60.94, 119.72) * mm, "end": v(-48.24, 119.72) * mm, "construction": true});
            skLineSegment(sketch, "E49", {"start": v(-52.9, 111.67) * mm, "end": v(-52.9, 107.02) * mm});
            skLineSegment(sketch, "E50", {"start": v(-52.9, 107.02) * mm, "end": v(-48.24, 107.02) * mm});
            skLineSegment(sketch, "E51", {"start": v(-48.24, 107.02) * mm, "end": v(-48.24, 111.67) * mm});
            skLineSegment(sketch, "E52", {"start": v(-48.24, 111.67) * mm, "end": v(-52.9, 111.67) * mm});
            skLineSegment(sketch, "E53.0.1.0", {"start": v(-52.9, 94.32) * mm, "end": v(-48.24, 94.32) * mm});
            skLineSegment(sketch, "E53.0.1.1", {"start": v(-48.24, 94.32) * mm, "end": v(-48.24, 98.97) * mm});
            skLineSegment(sketch, "E53.0.1.2", {"start": v(-52.9, 98.97) * mm, "end": v(-52.9, 94.32) * mm});
            skLineSegment(sketch, "E53.0.1.3", {"start": v(-48.24, 98.97) * mm, "end": v(-52.9, 98.97) * mm});
            skLineSegment(sketch, "E53.0.2.0", {"start": v(-52.9, 81.62) * mm, "end": v(-48.24, 81.62) * mm});
            skLineSegment(sketch, "E53.0.2.1", {"start": v(-48.24, 81.62) * mm, "end": v(-48.24, 86.27) * mm});
            skLineSegment(sketch, "E53.0.2.2", {"start": v(-52.9, 86.27) * mm, "end": v(-52.9, 81.62) * mm});
            skLineSegment(sketch, "E53.0.2.3", {"start": v(-48.24, 86.27) * mm, "end": v(-52.9, 86.27) * mm});
            skLineSegment(sketch, "E53.0.3.0", {"start": v(-52.9, 68.92) * mm, "end": v(-48.24, 68.92) * mm});
            skLineSegment(sketch, "E53.0.3.1", {"start": v(-48.24, 68.92) * mm, "end": v(-48.24, 73.57) * mm});
            skLineSegment(sketch, "E53.0.3.2", {"start": v(-52.9, 73.57) * mm, "end": v(-52.9, 68.92) * mm});
            skLineSegment(sketch, "E53.0.3.3", {"start": v(-48.24, 73.57) * mm, "end": v(-52.9, 73.57) * mm});
            skLineSegment(sketch, "E53.0.4.0", {"start": v(-52.9, 56.22) * mm, "end": v(-48.24, 56.22) * mm});
            skLineSegment(sketch, "E53.0.4.1", {"start": v(-48.24, 56.22) * mm, "end": v(-48.24, 60.87) * mm});
            skLineSegment(sketch, "E53.0.4.2", {"start": v(-52.9, 60.87) * mm, "end": v(-52.9, 56.22) * mm});
            skLineSegment(sketch, "E53.0.4.3", {"start": v(-48.24, 60.87) * mm, "end": v(-52.9, 60.87) * mm});
            skLineSegment(sketch, "E53.0.5.0", {"start": v(-52.9, 43.52) * mm, "end": v(-48.24, 43.52) * mm});
            skLineSegment(sketch, "E53.0.5.1", {"start": v(-48.24, 43.52) * mm, "end": v(-48.24, 48.17) * mm});
            skLineSegment(sketch, "E53.0.5.2", {"start": v(-52.9, 48.17) * mm, "end": v(-52.9, 43.52) * mm});
            skLineSegment(sketch, "E53.0.5.3", {"start": v(-48.24, 48.17) * mm, "end": v(-52.9, 48.17) * mm});
            skLineSegment(sketch, "E53.0.6.0", {"start": v(-52.9, 30.82) * mm, "end": v(-48.24, 30.82) * mm});
            skLineSegment(sketch, "E53.0.6.1", {"start": v(-48.24, 30.82) * mm, "end": v(-48.24, 35.47) * mm});
            skLineSegment(sketch, "E53.0.6.2", {"start": v(-52.9, 35.47) * mm, "end": v(-52.9, 30.82) * mm});
            skLineSegment(sketch, "E53.0.6.3", {"start": v(-48.24, 35.47) * mm, "end": v(-52.9, 35.47) * mm});
            skLineSegment(sketch, "E53.0.7.0", {"start": v(-52.9, 18.12) * mm, "end": v(-48.24, 18.12) * mm});
            skLineSegment(sketch, "E53.0.7.1", {"start": v(-48.24, 18.12) * mm, "end": v(-48.24, 22.77) * mm});
            skLineSegment(sketch, "E53.0.7.2", {"start": v(-52.9, 22.77) * mm, "end": v(-52.9, 18.12) * mm});
            skLineSegment(sketch, "E53.0.7.3", {"start": v(-48.24, 22.77) * mm, "end": v(-52.9, 22.77) * mm});
            skLineSegment(sketch, "E53.0.8.0", {"start": v(-52.9, 5.42) * mm, "end": v(-48.24, 5.42) * mm});
            skLineSegment(sketch, "E53.0.8.1", {"start": v(-48.24, 5.42) * mm, "end": v(-48.24, 10.07) * mm});
            skLineSegment(sketch, "E53.0.8.2", {"start": v(-52.9, 10.07) * mm, "end": v(-52.9, 5.42) * mm});
            skLineSegment(sketch, "E53.0.8.3", {"start": v(-48.24, 10.07) * mm, "end": v(-52.9, 10.07) * mm});
            skLineSegment(sketch, "E53.0.9.0", {"start": v(-52.9, -7.28) * mm, "end": v(-48.24, -7.28) * mm});
            skLineSegment(sketch, "E53.0.9.1", {"start": v(-48.24, -7.28) * mm, "end": v(-48.24, -2.63) * mm});
            skLineSegment(sketch, "E53.0.9.2", {"start": v(-52.9, -2.63) * mm, "end": v(-52.9, -7.28) * mm});
            skLineSegment(sketch, "E53.0.9.3", {"start": v(-48.24, -2.63) * mm, "end": v(-52.9, -2.63) * mm});
            skLineSegment(sketch, "E53.0.10.0", {"start": v(-52.9, -19.98) * mm, "end": v(-48.24, -19.98) * mm});
            skLineSegment(sketch, "E53.0.10.1", {"start": v(-48.24, -19.98) * mm, "end": v(-48.24, -15.33) * mm});
            skLineSegment(sketch, "E53.0.10.2", {"start": v(-52.9, -15.33) * mm, "end": v(-52.9, -19.98) * mm});
            skLineSegment(sketch, "E53.0.10.3", {"start": v(-48.24, -15.33) * mm, "end": v(-52.9, -15.33) * mm});
            skLineSegment(sketch, "E53.0.11.0", {"start": v(-52.9, -32.68) * mm, "end": v(-48.24, -32.68) * mm});
            skLineSegment(sketch, "E53.0.11.1", {"start": v(-48.24, -32.68) * mm, "end": v(-48.24, -28.03) * mm});
            skLineSegment(sketch, "E53.0.11.2", {"start": v(-52.9, -28.03) * mm, "end": v(-52.9, -32.68) * mm});
            skLineSegment(sketch, "E53.0.11.3", {"start": v(-48.24, -28.03) * mm, "end": v(-52.9, -28.03) * mm});
            skLineSegment(sketch, "E53.direction1", {"start": v(-52.9, 107.02) * mm, "end": v(-40.2, 107.02) * mm, "construction": true});
            skLineSegment(sketch, "E53.direction2", {"start": v(-52.9, 107.02) * mm, "end": v(-52.9, 94.32) * mm, "construction": true});
            skLineSegment(sketch, "E54", {"start": v(116.86, 119.72) * mm, "end": v(116.86, 111.67) * mm});
            skLineSegment(sketch, "E55", {"start": v(116.86, 111.67) * mm, "end": v(116.86, 107.05) * mm});
            skLineSegment(sketch, "E56", {"start": v(116.86, 107.05) * mm, "end": v(112.2, 107.05) * mm});
            skLineSegment(sketch, "E57", {"start": v(116.86, 111.67) * mm, "end": v(112.2, 111.67) * mm});
            skLineSegment(sketch, "E58", {"start": v(112.2, 111.67) * mm, "end": v(112.2, 107.05) * mm});
            skLineSegment(sketch, "E59.0.1.0", {"start": v(116.86, 98.97) * mm, "end": v(116.86, 94.35) * mm});
            skLineSegment(sketch, "E59.0.1.1", {"start": v(116.86, 98.97) * mm, "end": v(112.2, 98.97) * mm});
            skLineSegment(sketch, "E59.0.1.2", {"start": v(112.2, 98.97) * mm, "end": v(112.2, 94.35) * mm});
            skLineSegment(sketch, "E59.0.1.3", {"start": v(116.86, 94.35) * mm, "end": v(112.2, 94.35) * mm});
            skLineSegment(sketch, "E59.0.2.0", {"start": v(116.86, 86.27) * mm, "end": v(116.86, 81.65) * mm});
            skLineSegment(sketch, "E59.0.2.1", {"start": v(116.86, 86.27) * mm, "end": v(112.2, 86.27) * mm});
            skLineSegment(sketch, "E59.0.2.2", {"start": v(112.2, 86.27) * mm, "end": v(112.2, 81.65) * mm});
            skLineSegment(sketch, "E59.0.2.3", {"start": v(116.86, 81.65) * mm, "end": v(112.2, 81.65) * mm});
            skLineSegment(sketch, "E59.0.3.0", {"start": v(116.86, 73.57) * mm, "end": v(116.86, 68.95) * mm});
            skLineSegment(sketch, "E59.0.3.1", {"start": v(116.86, 73.57) * mm, "end": v(112.2, 73.57) * mm});
            skLineSegment(sketch, "E59.0.3.2", {"start": v(112.2, 73.57) * mm, "end": v(112.2, 68.95) * mm});
            skLineSegment(sketch, "E59.0.3.3", {"start": v(116.86, 68.95) * mm, "end": v(112.2, 68.95) * mm});
            skLineSegment(sketch, "E59.0.4.0", {"start": v(116.86, 60.87) * mm, "end": v(116.86, 56.25) * mm});
            skLineSegment(sketch, "E59.0.4.1", {"start": v(116.86, 60.87) * mm, "end": v(112.2, 60.87) * mm});
            skLineSegment(sketch, "E59.0.4.2", {"start": v(112.2, 60.87) * mm, "end": v(112.2, 56.25) * mm});
            skLineSegment(sketch, "E59.0.4.3", {"start": v(116.86, 56.25) * mm, "end": v(112.2, 56.25) * mm});
            skLineSegment(sketch, "E59.0.5.0", {"start": v(116.86, 48.17) * mm, "end": v(116.86, 43.55) * mm});
            skLineSegment(sketch, "E59.0.5.1", {"start": v(116.86, 48.17) * mm, "end": v(112.2, 48.17) * mm});
            skLineSegment(sketch, "E59.0.5.2", {"start": v(112.2, 48.17) * mm, "end": v(112.2, 43.55) * mm});
            skLineSegment(sketch, "E59.0.5.3", {"start": v(116.86, 43.55) * mm, "end": v(112.2, 43.55) * mm});
            skLineSegment(sketch, "E59.0.6.0", {"start": v(116.86, 35.47) * mm, "end": v(116.86, 30.85) * mm});
            skLineSegment(sketch, "E59.0.6.1", {"start": v(116.86, 35.47) * mm, "end": v(112.2, 35.47) * mm});
            skLineSegment(sketch, "E59.0.6.2", {"start": v(112.2, 35.47) * mm, "end": v(112.2, 30.85) * mm});
            skLineSegment(sketch, "E59.0.6.3", {"start": v(116.86, 30.85) * mm, "end": v(112.2, 30.85) * mm});
            skLineSegment(sketch, "E59.0.7.0", {"start": v(116.86, 22.77) * mm, "end": v(116.86, 18.15) * mm});
            skLineSegment(sketch, "E59.0.7.1", {"start": v(116.86, 22.77) * mm, "end": v(112.2, 22.77) * mm});
            skLineSegment(sketch, "E59.0.7.2", {"start": v(112.2, 22.77) * mm, "end": v(112.2, 18.15) * mm});
            skLineSegment(sketch, "E59.0.7.3", {"start": v(116.86, 18.15) * mm, "end": v(112.2, 18.15) * mm});
            skLineSegment(sketch, "E59.0.8.0", {"start": v(116.86, 10.07) * mm, "end": v(116.86, 5.45) * mm});
            skLineSegment(sketch, "E59.0.8.1", {"start": v(116.86, 10.07) * mm, "end": v(112.2, 10.07) * mm});
            skLineSegment(sketch, "E59.0.8.2", {"start": v(112.2, 10.07) * mm, "end": v(112.2, 5.45) * mm});
            skLineSegment(sketch, "E59.0.8.3", {"start": v(116.86, 5.45) * mm, "end": v(112.2, 5.45) * mm});
            skLineSegment(sketch, "E59.0.9.0", {"start": v(116.86, -2.63) * mm, "end": v(116.86, -7.25) * mm});
            skLineSegment(sketch, "E59.0.9.1", {"start": v(116.86, -2.63) * mm, "end": v(112.2, -2.63) * mm});
            skLineSegment(sketch, "E59.0.9.2", {"start": v(112.2, -2.63) * mm, "end": v(112.2, -7.25) * mm});
            skLineSegment(sketch, "E59.0.9.3", {"start": v(116.86, -7.25) * mm, "end": v(112.2, -7.25) * mm});
            skLineSegment(sketch, "E59.0.10.0", {"start": v(116.86, -15.33) * mm, "end": v(116.86, -19.95) * mm});
            skLineSegment(sketch, "E59.0.10.1", {"start": v(116.86, -15.33) * mm, "end": v(112.2, -15.33) * mm});
            skLineSegment(sketch, "E59.0.10.2", {"start": v(112.2, -15.33) * mm, "end": v(112.2, -19.95) * mm});
            skLineSegment(sketch, "E59.0.10.3", {"start": v(116.86, -19.95) * mm, "end": v(112.2, -19.95) * mm});
            skLineSegment(sketch, "E59.0.11.0", {"start": v(116.86, -28.03) * mm, "end": v(116.86, -32.65) * mm});
            skLineSegment(sketch, "E59.0.11.1", {"start": v(116.86, -28.03) * mm, "end": v(112.2, -28.03) * mm});
            skLineSegment(sketch, "E59.0.11.2", {"start": v(112.2, -28.03) * mm, "end": v(112.2, -32.65) * mm});
            skLineSegment(sketch, "E59.0.11.3", {"start": v(116.86, -32.65) * mm, "end": v(112.2, -32.65) * mm});
            skLineSegment(sketch, "E59.direction1", {"start": v(116.86, 107.05) * mm, "end": v(142.26, 107.05) * mm, "construction": true});
            skLineSegment(sketch, "E59.direction2", {"start": v(116.86, 107.05) * mm, "end": v(116.86, 94.35) * mm, "construction": true});
            skLineSegment(sketch, "E60.0.1.0", {"start": v(-40.2, 107.02) * mm, "end": v(-35.54, 107.02) * mm});
            skLineSegment(sketch, "E60.3.1.0", {"start": v(-35.54, 107.02) * mm, "end": v(-35.54, 111.67) * mm});
            skLineSegment(sketch, "E60.6.1.0", {"start": v(-40.2, 111.67) * mm, "end": v(-40.2, 107.02) * mm});
            skLineSegment(sketch, "E60.9.1.0", {"start": v(-35.54, 111.67) * mm, "end": v(-40.2, 111.67) * mm});
            skLineSegment(sketch, "E60.0.1.1", {"start": v(-40.2, 94.32) * mm, "end": v(-35.54, 94.32) * mm});
            skLineSegment(sketch, "E60.3.1.1", {"start": v(-35.54, 94.32) * mm, "end": v(-35.54, 98.97) * mm});
            skLineSegment(sketch, "E60.6.1.1", {"start": v(-40.2, 98.97) * mm, "end": v(-40.2, 94.32) * mm});
            skLineSegment(sketch, "E60.9.1.1", {"start": v(-35.54, 98.97) * mm, "end": v(-40.2, 98.97) * mm});
            skLineSegment(sketch, "E60.0.1.2", {"start": v(-40.2, 81.62) * mm, "end": v(-35.54, 81.62) * mm});
            skLineSegment(sketch, "E60.3.1.2", {"start": v(-35.54, 81.62) * mm, "end": v(-35.54, 86.27) * mm});
            skLineSegment(sketch, "E60.6.1.2", {"start": v(-40.2, 86.27) * mm, "end": v(-40.2, 81.62) * mm});
            skLineSegment(sketch, "E60.9.1.2", {"start": v(-35.54, 86.27) * mm, "end": v(-40.2, 86.27) * mm});
            skLineSegment(sketch, "E60.0.1.3", {"start": v(-40.2, 68.92) * mm, "end": v(-35.54, 68.92) * mm});
            skLineSegment(sketch, "E60.3.1.3", {"start": v(-35.54, 68.92) * mm, "end": v(-35.54, 73.57) * mm});
            skLineSegment(sketch, "E60.6.1.3", {"start": v(-40.2, 73.57) * mm, "end": v(-40.2, 68.92) * mm});
            skLineSegment(sketch, "E60.9.1.3", {"start": v(-35.54, 73.57) * mm, "end": v(-40.2, 73.57) * mm});
            skLineSegment(sketch, "E60.0.1.4", {"start": v(-40.2, 56.22) * mm, "end": v(-35.54, 56.22) * mm});
            skLineSegment(sketch, "E60.3.1.4", {"start": v(-35.54, 56.22) * mm, "end": v(-35.54, 60.87) * mm});
            skLineSegment(sketch, "E60.6.1.4", {"start": v(-40.2, 60.87) * mm, "end": v(-40.2, 56.22) * mm});
            skLineSegment(sketch, "E60.9.1.4", {"start": v(-35.54, 60.87) * mm, "end": v(-40.2, 60.87) * mm});
            skLineSegment(sketch, "E60.0.1.5", {"start": v(-40.2, 43.52) * mm, "end": v(-35.54, 43.52) * mm});
            skLineSegment(sketch, "E60.3.1.5", {"start": v(-35.54, 43.52) * mm, "end": v(-35.54, 48.17) * mm});
            skLineSegment(sketch, "E60.6.1.5", {"start": v(-40.2, 48.17) * mm, "end": v(-40.2, 43.52) * mm});
            skLineSegment(sketch, "E60.9.1.5", {"start": v(-35.54, 48.17) * mm, "end": v(-40.2, 48.17) * mm});
            skLineSegment(sketch, "E60.0.1.6", {"start": v(-40.2, 30.82) * mm, "end": v(-35.54, 30.82) * mm});
            skLineSegment(sketch, "E60.3.1.6", {"start": v(-35.54, 30.82) * mm, "end": v(-35.54, 35.47) * mm});
            skLineSegment(sketch, "E60.6.1.6", {"start": v(-40.2, 35.47) * mm, "end": v(-40.2, 30.82) * mm});
            skLineSegment(sketch, "E60.9.1.6", {"start": v(-35.54, 35.47) * mm, "end": v(-40.2, 35.47) * mm});
            skLineSegment(sketch, "E60.0.1.7", {"start": v(-40.2, 18.12) * mm, "end": v(-35.54, 18.12) * mm});
            skLineSegment(sketch, "E60.3.1.7", {"start": v(-35.54, 18.12) * mm, "end": v(-35.54, 22.77) * mm});
            skLineSegment(sketch, "E60.6.1.7", {"start": v(-40.2, 22.77) * mm, "end": v(-40.2, 18.12) * mm});
            skLineSegment(sketch, "E60.9.1.7", {"start": v(-35.54, 22.77) * mm, "end": v(-40.2, 22.77) * mm});
            skLineSegment(sketch, "E60.0.1.8", {"start": v(-40.2, 5.42) * mm, "end": v(-35.54, 5.42) * mm});
            skLineSegment(sketch, "E60.3.1.8", {"start": v(-35.54, 5.42) * mm, "end": v(-35.54, 10.07) * mm});
            skLineSegment(sketch, "E60.6.1.8", {"start": v(-40.2, 10.07) * mm, "end": v(-40.2, 5.42) * mm});
            skLineSegment(sketch, "E60.9.1.8", {"start": v(-35.54, 10.07) * mm, "end": v(-40.2, 10.07) * mm});
            skLineSegment(sketch, "E60.0.1.9", {"start": v(-40.2, -7.28) * mm, "end": v(-35.54, -7.28) * mm});
            skLineSegment(sketch, "E60.3.1.9", {"start": v(-35.54, -7.28) * mm, "end": v(-35.54, -2.63) * mm});
            skLineSegment(sketch, "E60.6.1.9", {"start": v(-40.2, -2.63) * mm, "end": v(-40.2, -7.28) * mm});
            skLineSegment(sketch, "E60.9.1.9", {"start": v(-35.54, -2.63) * mm, "end": v(-40.2, -2.63) * mm});
            skLineSegment(sketch, "E60.0.1.10", {"start": v(-40.2, -19.98) * mm, "end": v(-35.54, -19.98) * mm});
            skLineSegment(sketch, "E60.3.1.10", {"start": v(-35.54, -19.98) * mm, "end": v(-35.54, -15.33) * mm});
            skLineSegment(sketch, "E60.6.1.10", {"start": v(-40.2, -15.33) * mm, "end": v(-40.2, -19.98) * mm});
            skLineSegment(sketch, "E60.9.1.10", {"start": v(-35.54, -15.33) * mm, "end": v(-40.2, -15.33) * mm});
            skLineSegment(sketch, "E60.0.1.11", {"start": v(-40.2, -32.68) * mm, "end": v(-35.54, -32.68) * mm});
            skLineSegment(sketch, "E60.3.1.11", {"start": v(-35.54, -32.68) * mm, "end": v(-35.54, -28.03) * mm});
            skLineSegment(sketch, "E60.6.1.11", {"start": v(-40.2, -28.03) * mm, "end": v(-40.2, -32.68) * mm});
            skLineSegment(sketch, "E60.9.1.11", {"start": v(-35.54, -28.03) * mm, "end": v(-40.2, -28.03) * mm});
            skLineSegment(sketch, "E61.0.1.0", {"start": v(104.16, 107.02) * mm, "end": v(99.5, 107.02) * mm});
            skLineSegment(sketch, "E61.0.1.1", {"start": v(99.5, 111.67) * mm, "end": v(99.5, 107.02) * mm});
            skLineSegment(sketch, "E61.0.1.2", {"start": v(104.16, 111.67) * mm, "end": v(99.5, 111.67) * mm});
            skLineSegment(sketch, "E61.0.1.3", {"start": v(104.16, 111.67) * mm, "end": v(104.16, 107.02) * mm});
            skLineSegment(sketch, "E61.0.2.0", {"start": v(104.16, 94.32) * mm, "end": v(99.5, 94.32) * mm});
            skLineSegment(sketch, "E61.0.2.1", {"start": v(99.5, 98.97) * mm, "end": v(99.5, 94.32) * mm});
            skLineSegment(sketch, "E61.0.2.2", {"start": v(104.16, 98.97) * mm, "end": v(99.5, 98.97) * mm});
            skLineSegment(sketch, "E61.0.2.3", {"start": v(104.16, 98.97) * mm, "end": v(104.16, 94.32) * mm});
            skLineSegment(sketch, "E61.0.3.0", {"start": v(104.16, 81.62) * mm, "end": v(99.5, 81.62) * mm});
            skLineSegment(sketch, "E61.0.3.1", {"start": v(99.5, 86.27) * mm, "end": v(99.5, 81.62) * mm});
            skLineSegment(sketch, "E61.0.3.2", {"start": v(104.16, 86.27) * mm, "end": v(99.5, 86.27) * mm});
            skLineSegment(sketch, "E61.0.3.3", {"start": v(104.16, 86.27) * mm, "end": v(104.16, 81.62) * mm});
            skLineSegment(sketch, "E61.0.4.0", {"start": v(104.16, 68.92) * mm, "end": v(99.5, 68.92) * mm});
            skLineSegment(sketch, "E61.0.4.1", {"start": v(99.5, 73.57) * mm, "end": v(99.5, 68.92) * mm});
            skLineSegment(sketch, "E61.0.4.2", {"start": v(104.16, 73.57) * mm, "end": v(99.5, 73.57) * mm});
            skLineSegment(sketch, "E61.0.4.3", {"start": v(104.16, 73.57) * mm, "end": v(104.16, 68.92) * mm});
            skLineSegment(sketch, "E61.0.5.0", {"start": v(104.16, 56.22) * mm, "end": v(99.5, 56.22) * mm});
            skLineSegment(sketch, "E61.0.5.1", {"start": v(99.5, 60.87) * mm, "end": v(99.5, 56.22) * mm});
            skLineSegment(sketch, "E61.0.5.2", {"start": v(104.16, 60.87) * mm, "end": v(99.5, 60.87) * mm});
            skLineSegment(sketch, "E61.0.5.3", {"start": v(104.16, 60.87) * mm, "end": v(104.16, 56.22) * mm});
            skLineSegment(sketch, "E61.0.6.0", {"start": v(104.16, 43.52) * mm, "end": v(99.5, 43.52) * mm});
            skLineSegment(sketch, "E61.0.6.1", {"start": v(99.5, 48.17) * mm, "end": v(99.5, 43.52) * mm});
            skLineSegment(sketch, "E61.0.6.2", {"start": v(104.16, 48.17) * mm, "end": v(99.5, 48.17) * mm});
            skLineSegment(sketch, "E61.0.6.3", {"start": v(104.16, 48.17) * mm, "end": v(104.16, 43.52) * mm});
            skLineSegment(sketch, "E61.0.7.0", {"start": v(104.16, 30.82) * mm, "end": v(99.5, 30.82) * mm});
            skLineSegment(sketch, "E61.0.7.1", {"start": v(99.5, 35.47) * mm, "end": v(99.5, 30.82) * mm});
            skLineSegment(sketch, "E61.0.7.2", {"start": v(104.16, 35.47) * mm, "end": v(99.5, 35.47) * mm});
            skLineSegment(sketch, "E61.0.7.3", {"start": v(104.16, 35.47) * mm, "end": v(104.16, 30.82) * mm});
            skLineSegment(sketch, "E61.0.8.0", {"start": v(104.16, 18.12) * mm, "end": v(99.5, 18.12) * mm});
            skLineSegment(sketch, "E61.0.8.1", {"start": v(99.5, 22.77) * mm, "end": v(99.5, 18.12) * mm});
            skLineSegment(sketch, "E61.0.8.2", {"start": v(104.16, 22.77) * mm, "end": v(99.5, 22.77) * mm});
            skLineSegment(sketch, "E61.0.8.3", {"start": v(104.16, 22.77) * mm, "end": v(104.16, 18.12) * mm});
            skLineSegment(sketch, "E61.0.9.0", {"start": v(104.16, 5.42) * mm, "end": v(99.5, 5.42) * mm});
            skLineSegment(sketch, "E61.0.9.1", {"start": v(99.5, 10.07) * mm, "end": v(99.5, 5.42) * mm});
            skLineSegment(sketch, "E61.0.9.2", {"start": v(104.16, 10.07) * mm, "end": v(99.5, 10.07) * mm});
            skLineSegment(sketch, "E61.0.9.3", {"start": v(104.16, 10.07) * mm, "end": v(104.16, 5.42) * mm});
            skLineSegment(sketch, "E61.0.10.0", {"start": v(104.16, -7.28) * mm, "end": v(99.5, -7.28) * mm});
            skLineSegment(sketch, "E61.0.10.1", {"start": v(99.5, -2.63) * mm, "end": v(99.5, -7.28) * mm});
            skLineSegment(sketch, "E61.0.10.2", {"start": v(104.16, -2.63) * mm, "end": v(99.5, -2.63) * mm});
            skLineSegment(sketch, "E61.0.10.3", {"start": v(104.16, -2.63) * mm, "end": v(104.16, -7.28) * mm});
            skLineSegment(sketch, "E61.0.11.0", {"start": v(104.16, -19.98) * mm, "end": v(99.5, -19.98) * mm});
            skLineSegment(sketch, "E61.0.11.1", {"start": v(99.5, -15.33) * mm, "end": v(99.5, -19.98) * mm});
            skLineSegment(sketch, "E61.0.11.2", {"start": v(104.16, -15.33) * mm, "end": v(99.5, -15.33) * mm});
            skLineSegment(sketch, "E61.0.11.3", {"start": v(104.16, -15.33) * mm, "end": v(104.16, -19.98) * mm});
            skLineSegment(sketch, "E61.0.12.0", {"start": v(104.16, -32.68) * mm, "end": v(99.5, -32.68) * mm});
            skLineSegment(sketch, "E61.0.12.1", {"start": v(99.5, -28.03) * mm, "end": v(99.5, -32.68) * mm});
            skLineSegment(sketch, "E61.0.12.2", {"start": v(104.16, -28.03) * mm, "end": v(99.5, -28.03) * mm});
            skLineSegment(sketch, "E61.0.12.3", {"start": v(104.16, -28.03) * mm, "end": v(104.16, -32.68) * mm});
            skLineSegment(sketch, "E61.direction1", {"start": v(99.5, 119.72) * mm, "end": v(124.9, 119.72) * mm, "construction": true});
            skLineSegment(sketch, "E61.direction2", {"start": v(99.5, 119.72) * mm, "end": v(99.5, 107.02) * mm, "construction": true});
            skLineSegment(sketch, "E62", {"start": v(-27.5, 111.67) * mm, "end": v(-22.84, 111.67) * mm});
            skSolve(sketch);
        }
        {
            var Q0;
            Q0=qCreatedBy(makeId("Right.planeOp"),FACE);
            var sketch = newSketch(context, id + "F1", { "sketchPlane" : qUnion([Q0])});
            skLineSegment(sketch, "E63", {"start": v(110.96, 0) * mm, "end": v(110.96, 63.25) * mm});
            skLineSegment(sketch, "E64", {"start": v(-92.24, 63.25) * mm, "end": v(-92.24, 0) * mm});
            skLineSegment(sketch, "E65", {"start": v(110.96, 63.25) * mm, "end": v(-92.24, 63.25) * mm});
            skLineSegment(sketch, "E66", {"start": v(110.96, 0) * mm, "end": v(-92.24, 0) * mm});
            skLineSegment(sketch, "E67.bottom", {"start": v(107.05, 59.33) * mm, "end": v(102.43, 59.33) * mm});
            skLineSegment(sketch, "E67.top", {"start": v(107.05, 54.71) * mm, "end": v(102.43, 54.71) * mm});
            skLineSegment(sketch, "E67.left", {"start": v(107.05, 59.33) * mm, "end": v(107.05, 54.71) * mm});
            skLineSegment(sketch, "E67.right", {"start": v(102.43, 59.33) * mm, "end": v(102.43, 54.71) * mm});
            skLineSegment(sketch, "E68.0.1.0", {"start": v(107.05, 42.01) * mm, "end": v(102.43, 42.01) * mm});
            skLineSegment(sketch, "E68.0.1.1", {"start": v(107.05, 46.63) * mm, "end": v(107.05, 42.01) * mm});
            skLineSegment(sketch, "E68.0.1.2", {"start": v(107.05, 46.63) * mm, "end": v(102.43, 46.63) * mm});
            skLineSegment(sketch, "E68.0.1.3", {"start": v(102.43, 46.63) * mm, "end": v(102.43, 42.01) * mm});
            skLineSegment(sketch, "E68.0.2.0", {"start": v(107.05, 29.31) * mm, "end": v(102.43, 29.31) * mm});
            skLineSegment(sketch, "E68.0.2.1", {"start": v(107.05, 33.93) * mm, "end": v(107.05, 29.31) * mm});
            skLineSegment(sketch, "E68.0.2.2", {"start": v(107.05, 33.93) * mm, "end": v(102.43, 33.93) * mm});
            skLineSegment(sketch, "E68.0.2.3", {"start": v(102.43, 33.93) * mm, "end": v(102.43, 29.31) * mm});
            skLineSegment(sketch, "E68.0.3.0", {"start": v(107.05, 16.61) * mm, "end": v(102.43, 16.61) * mm});
            skLineSegment(sketch, "E68.0.3.1", {"start": v(107.05, 21.23) * mm, "end": v(107.05, 16.61) * mm});
            skLineSegment(sketch, "E68.0.3.2", {"start": v(107.05, 21.23) * mm, "end": v(102.43, 21.23) * mm});
            skLineSegment(sketch, "E68.0.3.3", {"start": v(102.43, 21.23) * mm, "end": v(102.43, 16.61) * mm});
            skLineSegment(sketch, "E68.0.4.0", {"start": v(107.05, 3.91) * mm, "end": v(102.43, 3.91) * mm});
            skLineSegment(sketch, "E68.0.4.1", {"start": v(107.05, 8.53) * mm, "end": v(107.05, 3.91) * mm});
            skLineSegment(sketch, "E68.0.4.2", {"start": v(107.05, 8.53) * mm, "end": v(102.43, 8.53) * mm});
            skLineSegment(sketch, "E68.0.4.3", {"start": v(102.43, 8.53) * mm, "end": v(102.43, 3.91) * mm});
            skLineSegment(sketch, "E68.1.0.0", {"start": v(94.35, 54.71) * mm, "end": v(89.73, 54.71) * mm});
            skLineSegment(sketch, "E68.1.0.1", {"start": v(94.35, 59.33) * mm, "end": v(94.35, 54.71) * mm});
            skLineSegment(sketch, "E68.1.0.2", {"start": v(94.35, 59.33) * mm, "end": v(89.73, 59.33) * mm});
            skLineSegment(sketch, "E68.1.0.3", {"start": v(89.73, 59.33) * mm, "end": v(89.73, 54.71) * mm});
            skLineSegment(sketch, "E68.1.1.0", {"start": v(94.35, 42.01) * mm, "end": v(89.73, 42.01) * mm});
            skLineSegment(sketch, "E68.1.1.1", {"start": v(94.35, 46.63) * mm, "end": v(94.35, 42.01) * mm});
            skLineSegment(sketch, "E68.1.1.2", {"start": v(94.35, 46.63) * mm, "end": v(89.73, 46.63) * mm});
            skLineSegment(sketch, "E68.1.1.3", {"start": v(89.73, 46.63) * mm, "end": v(89.73, 42.01) * mm});
            skLineSegment(sketch, "E68.1.2.0", {"start": v(94.35, 29.31) * mm, "end": v(89.73, 29.31) * mm});
            skLineSegment(sketch, "E68.1.2.1", {"start": v(94.35, 33.93) * mm, "end": v(94.35, 29.31) * mm});
            skLineSegment(sketch, "E68.1.2.2", {"start": v(94.35, 33.93) * mm, "end": v(89.73, 33.93) * mm});
            skLineSegment(sketch, "E68.1.2.3", {"start": v(89.73, 33.93) * mm, "end": v(89.73, 29.31) * mm});
            skLineSegment(sketch, "E68.1.3.0", {"start": v(94.35, 16.61) * mm, "end": v(89.73, 16.61) * mm});
            skLineSegment(sketch, "E68.1.3.1", {"start": v(94.35, 21.23) * mm, "end": v(94.35, 16.61) * mm});
            skLineSegment(sketch, "E68.1.3.2", {"start": v(94.35, 21.23) * mm, "end": v(89.73, 21.23) * mm});
            skLineSegment(sketch, "E68.1.3.3", {"start": v(89.73, 21.23) * mm, "end": v(89.73, 16.61) * mm});
            skLineSegment(sketch, "E68.1.4.0", {"start": v(94.35, 3.91) * mm, "end": v(89.73, 3.91) * mm});
            skLineSegment(sketch, "E68.1.4.1", {"start": v(94.35, 8.53) * mm, "end": v(94.35, 3.91) * mm});
            skLineSegment(sketch, "E68.1.4.2", {"start": v(94.35, 8.53) * mm, "end": v(89.73, 8.53) * mm});
            skLineSegment(sketch, "E68.1.4.3", {"start": v(89.73, 8.53) * mm, "end": v(89.73, 3.91) * mm});
            skLineSegment(sketch, "E68.2.0.0", {"start": v(81.65, 54.71) * mm, "end": v(77.03, 54.71) * mm});
            skLineSegment(sketch, "E68.2.0.1", {"start": v(81.65, 59.33) * mm, "end": v(81.65, 54.71) * mm});
            skLineSegment(sketch, "E68.2.0.2", {"start": v(81.65, 59.33) * mm, "end": v(77.03, 59.33) * mm});
            skLineSegment(sketch, "E68.2.0.3", {"start": v(77.03, 59.33) * mm, "end": v(77.03, 54.71) * mm});
            skLineSegment(sketch, "E68.2.1.0", {"start": v(81.65, 42.01) * mm, "end": v(77.03, 42.01) * mm});
            skLineSegment(sketch, "E68.2.1.1", {"start": v(81.65, 46.63) * mm, "end": v(81.65, 42.01) * mm});
            skLineSegment(sketch, "E68.2.1.2", {"start": v(81.65, 46.63) * mm, "end": v(77.03, 46.63) * mm});
            skLineSegment(sketch, "E68.2.1.3", {"start": v(77.03, 46.63) * mm, "end": v(77.03, 42.01) * mm});
            skLineSegment(sketch, "E68.2.2.0", {"start": v(81.65, 29.31) * mm, "end": v(77.03, 29.31) * mm});
            skLineSegment(sketch, "E68.2.2.1", {"start": v(81.65, 33.93) * mm, "end": v(81.65, 29.31) * mm});
            skLineSegment(sketch, "E68.2.2.2", {"start": v(81.65, 33.93) * mm, "end": v(77.03, 33.93) * mm});
            skLineSegment(sketch, "E68.2.2.3", {"start": v(77.03, 33.93) * mm, "end": v(77.03, 29.31) * mm});
            skLineSegment(sketch, "E68.2.3.0", {"start": v(81.65, 16.61) * mm, "end": v(77.03, 16.61) * mm});
            skLineSegment(sketch, "E68.2.3.1", {"start": v(81.65, 21.23) * mm, "end": v(81.65, 16.61) * mm});
            skLineSegment(sketch, "E68.2.3.2", {"start": v(81.65, 21.23) * mm, "end": v(77.03, 21.23) * mm});
            skLineSegment(sketch, "E68.2.3.3", {"start": v(77.03, 21.23) * mm, "end": v(77.03, 16.61) * mm});
            skLineSegment(sketch, "E68.2.4.0", {"start": v(81.65, 3.91) * mm, "end": v(77.03, 3.91) * mm});
            skLineSegment(sketch, "E68.2.4.1", {"start": v(81.65, 8.53) * mm, "end": v(81.65, 3.91) * mm});
            skLineSegment(sketch, "E68.2.4.2", {"start": v(81.65, 8.53) * mm, "end": v(77.03, 8.53) * mm});
            skLineSegment(sketch, "E68.2.4.3", {"start": v(77.03, 8.53) * mm, "end": v(77.03, 3.91) * mm});
            skLineSegment(sketch, "E68.3.0.0", {"start": v(68.95, 54.71) * mm, "end": v(64.33, 54.71) * mm});
            skLineSegment(sketch, "E68.3.0.1", {"start": v(68.95, 59.33) * mm, "end": v(68.95, 54.71) * mm});
            skLineSegment(sketch, "E68.3.0.2", {"start": v(68.95, 59.33) * mm, "end": v(64.33, 59.33) * mm});
            skLineSegment(sketch, "E68.3.0.3", {"start": v(64.33, 59.33) * mm, "end": v(64.33, 54.71) * mm});
            skLineSegment(sketch, "E68.3.1.0", {"start": v(68.95, 42.01) * mm, "end": v(64.33, 42.01) * mm});
            skLineSegment(sketch, "E68.3.1.1", {"start": v(68.95, 46.63) * mm, "end": v(68.95, 42.01) * mm});
            skLineSegment(sketch, "E68.3.1.2", {"start": v(68.95, 46.63) * mm, "end": v(64.33, 46.63) * mm});
            skLineSegment(sketch, "E68.3.1.3", {"start": v(64.33, 46.63) * mm, "end": v(64.33, 42.01) * mm});
            skLineSegment(sketch, "E68.3.2.0", {"start": v(68.95, 29.31) * mm, "end": v(64.33, 29.31) * mm});
            skLineSegment(sketch, "E68.3.2.1", {"start": v(68.95, 33.93) * mm, "end": v(68.95, 29.31) * mm});
            skLineSegment(sketch, "E68.3.2.2", {"start": v(68.95, 33.93) * mm, "end": v(64.33, 33.93) * mm});
            skLineSegment(sketch, "E68.3.2.3", {"start": v(64.33, 33.93) * mm, "end": v(64.33, 29.31) * mm});
            skLineSegment(sketch, "E68.3.3.0", {"start": v(68.95, 16.61) * mm, "end": v(64.33, 16.61) * mm});
            skLineSegment(sketch, "E68.3.3.1", {"start": v(68.95, 21.23) * mm, "end": v(68.95, 16.61) * mm});
            skLineSegment(sketch, "E68.3.3.2", {"start": v(68.95, 21.23) * mm, "end": v(64.33, 21.23) * mm});
            skLineSegment(sketch, "E68.3.3.3", {"start": v(64.33, 21.23) * mm, "end": v(64.33, 16.61) * mm});
            skLineSegment(sketch, "E68.3.4.0", {"start": v(68.95, 3.91) * mm, "end": v(64.33, 3.91) * mm});
            skLineSegment(sketch, "E68.3.4.1", {"start": v(68.95, 8.53) * mm, "end": v(68.95, 3.91) * mm});
            skLineSegment(sketch, "E68.3.4.2", {"start": v(68.95, 8.53) * mm, "end": v(64.33, 8.53) * mm});
            skLineSegment(sketch, "E68.3.4.3", {"start": v(64.33, 8.53) * mm, "end": v(64.33, 3.91) * mm});
            skLineSegment(sketch, "E68.4.0.0", {"start": v(56.25, 54.71) * mm, "end": v(51.63, 54.71) * mm});
            skLineSegment(sketch, "E68.4.0.1", {"start": v(56.25, 59.33) * mm, "end": v(56.25, 54.71) * mm});
            skLineSegment(sketch, "E68.4.0.2", {"start": v(56.25, 59.33) * mm, "end": v(51.63, 59.33) * mm});
            skLineSegment(sketch, "E68.4.0.3", {"start": v(51.63, 59.33) * mm, "end": v(51.63, 54.71) * mm});
            skLineSegment(sketch, "E68.4.1.0", {"start": v(56.25, 42.01) * mm, "end": v(51.63, 42.01) * mm});
            skLineSegment(sketch, "E68.4.1.1", {"start": v(56.25, 46.63) * mm, "end": v(56.25, 42.01) * mm});
            skLineSegment(sketch, "E68.4.1.2", {"start": v(56.25, 46.63) * mm, "end": v(51.63, 46.63) * mm});
            skLineSegment(sketch, "E68.4.1.3", {"start": v(51.63, 46.63) * mm, "end": v(51.63, 42.01) * mm});
            skLineSegment(sketch, "E68.4.2.0", {"start": v(56.25, 29.31) * mm, "end": v(51.63, 29.31) * mm});
            skLineSegment(sketch, "E68.4.2.1", {"start": v(56.25, 33.93) * mm, "end": v(56.25, 29.31) * mm});
            skLineSegment(sketch, "E68.4.2.2", {"start": v(56.25, 33.93) * mm, "end": v(51.63, 33.93) * mm});
            skLineSegment(sketch, "E68.4.2.3", {"start": v(51.63, 33.93) * mm, "end": v(51.63, 29.31) * mm});
            skLineSegment(sketch, "E68.4.3.0", {"start": v(56.25, 16.61) * mm, "end": v(51.63, 16.61) * mm});
            skLineSegment(sketch, "E68.4.3.1", {"start": v(56.25, 21.23) * mm, "end": v(56.25, 16.61) * mm});
            skLineSegment(sketch, "E68.4.3.2", {"start": v(56.25, 21.23) * mm, "end": v(51.63, 21.23) * mm});
            skLineSegment(sketch, "E68.4.3.3", {"start": v(51.63, 21.23) * mm, "end": v(51.63, 16.61) * mm});
            skLineSegment(sketch, "E68.4.4.0", {"start": v(56.25, 3.91) * mm, "end": v(51.63, 3.91) * mm});
            skLineSegment(sketch, "E68.4.4.1", {"start": v(56.25, 8.53) * mm, "end": v(56.25, 3.91) * mm});
            skLineSegment(sketch, "E68.4.4.2", {"start": v(56.25, 8.53) * mm, "end": v(51.63, 8.53) * mm});
            skLineSegment(sketch, "E68.4.4.3", {"start": v(51.63, 8.53) * mm, "end": v(51.63, 3.91) * mm});
            skLineSegment(sketch, "E68.5.0.0", {"start": v(43.55, 54.71) * mm, "end": v(38.93, 54.71) * mm});
            skLineSegment(sketch, "E68.5.0.1", {"start": v(43.55, 59.33) * mm, "end": v(43.55, 54.71) * mm});
            skLineSegment(sketch, "E68.5.0.2", {"start": v(43.55, 59.33) * mm, "end": v(38.93, 59.33) * mm});
            skLineSegment(sketch, "E68.5.0.3", {"start": v(38.93, 59.33) * mm, "end": v(38.93, 54.71) * mm});
            skLineSegment(sketch, "E68.5.1.0", {"start": v(43.55, 42.01) * mm, "end": v(38.93, 42.01) * mm});
            skLineSegment(sketch, "E68.5.1.1", {"start": v(43.55, 46.63) * mm, "end": v(43.55, 42.01) * mm});
            skLineSegment(sketch, "E68.5.1.2", {"start": v(43.55, 46.63) * mm, "end": v(38.93, 46.63) * mm});
            skLineSegment(sketch, "E68.5.1.3", {"start": v(38.93, 46.63) * mm, "end": v(38.93, 42.01) * mm});
            skLineSegment(sketch, "E68.5.2.0", {"start": v(43.55, 29.31) * mm, "end": v(38.93, 29.31) * mm});
            skLineSegment(sketch, "E68.5.2.1", {"start": v(43.55, 33.93) * mm, "end": v(43.55, 29.31) * mm});
            skLineSegment(sketch, "E68.5.2.2", {"start": v(43.55, 33.93) * mm, "end": v(38.93, 33.93) * mm});
            skLineSegment(sketch, "E68.5.2.3", {"start": v(38.93, 33.93) * mm, "end": v(38.93, 29.31) * mm});
            skLineSegment(sketch, "E68.5.3.0", {"start": v(43.55, 16.61) * mm, "end": v(38.93, 16.61) * mm});
            skLineSegment(sketch, "E68.5.3.1", {"start": v(43.55, 21.23) * mm, "end": v(43.55, 16.61) * mm});
            skLineSegment(sketch, "E68.5.3.2", {"start": v(43.55, 21.23) * mm, "end": v(38.93, 21.23) * mm});
            skLineSegment(sketch, "E68.5.3.3", {"start": v(38.93, 21.23) * mm, "end": v(38.93, 16.61) * mm});
            skLineSegment(sketch, "E68.5.4.0", {"start": v(43.55, 3.91) * mm, "end": v(38.93, 3.91) * mm});
            skLineSegment(sketch, "E68.5.4.1", {"start": v(43.55, 8.53) * mm, "end": v(43.55, 3.91) * mm});
            skLineSegment(sketch, "E68.5.4.2", {"start": v(43.55, 8.53) * mm, "end": v(38.93, 8.53) * mm});
            skLineSegment(sketch, "E68.5.4.3", {"start": v(38.93, 8.53) * mm, "end": v(38.93, 3.91) * mm});
            skLineSegment(sketch, "E68.6.0.0", {"start": v(30.85, 54.71) * mm, "end": v(26.23, 54.71) * mm});
            skLineSegment(sketch, "E68.6.0.1", {"start": v(30.85, 59.33) * mm, "end": v(30.85, 54.71) * mm});
            skLineSegment(sketch, "E68.6.0.2", {"start": v(30.85, 59.33) * mm, "end": v(26.23, 59.33) * mm});
            skLineSegment(sketch, "E68.6.0.3", {"start": v(26.23, 59.33) * mm, "end": v(26.23, 54.71) * mm});
            skLineSegment(sketch, "E68.6.1.0", {"start": v(30.85, 42.01) * mm, "end": v(26.23, 42.01) * mm});
            skLineSegment(sketch, "E68.6.1.1", {"start": v(30.85, 46.63) * mm, "end": v(30.85, 42.01) * mm});
            skLineSegment(sketch, "E68.6.1.2", {"start": v(30.85, 46.63) * mm, "end": v(26.23, 46.63) * mm});
            skLineSegment(sketch, "E68.6.1.3", {"start": v(26.23, 46.63) * mm, "end": v(26.23, 42.01) * mm});
            skLineSegment(sketch, "E68.6.2.0", {"start": v(30.85, 29.31) * mm, "end": v(26.23, 29.31) * mm});
            skLineSegment(sketch, "E68.6.2.1", {"start": v(30.85, 33.93) * mm, "end": v(30.85, 29.31) * mm});
            skLineSegment(sketch, "E68.6.2.2", {"start": v(30.85, 33.93) * mm, "end": v(26.23, 33.93) * mm});
            skLineSegment(sketch, "E68.6.2.3", {"start": v(26.23, 33.93) * mm, "end": v(26.23, 29.31) * mm});
            skLineSegment(sketch, "E68.6.3.0", {"start": v(30.85, 16.61) * mm, "end": v(26.23, 16.61) * mm});
            skLineSegment(sketch, "E68.6.3.1", {"start": v(30.85, 21.23) * mm, "end": v(30.85, 16.61) * mm});
            skLineSegment(sketch, "E68.6.3.2", {"start": v(30.85, 21.23) * mm, "end": v(26.23, 21.23) * mm});
            skLineSegment(sketch, "E68.6.3.3", {"start": v(26.23, 21.23) * mm, "end": v(26.23, 16.61) * mm});
            skLineSegment(sketch, "E68.6.4.0", {"start": v(30.85, 3.91) * mm, "end": v(26.23, 3.91) * mm});
            skLineSegment(sketch, "E68.6.4.1", {"start": v(30.85, 8.53) * mm, "end": v(30.85, 3.91) * mm});
            skLineSegment(sketch, "E68.6.4.2", {"start": v(30.85, 8.53) * mm, "end": v(26.23, 8.53) * mm});
            skLineSegment(sketch, "E68.6.4.3", {"start": v(26.23, 8.53) * mm, "end": v(26.23, 3.91) * mm});
            skLineSegment(sketch, "E68.7.0.0", {"start": v(18.15, 54.71) * mm, "end": v(13.53, 54.71) * mm});
            skLineSegment(sketch, "E68.7.0.1", {"start": v(18.15, 59.33) * mm, "end": v(18.15, 54.71) * mm});
            skLineSegment(sketch, "E68.7.0.2", {"start": v(18.15, 59.33) * mm, "end": v(13.53, 59.33) * mm});
            skLineSegment(sketch, "E68.7.0.3", {"start": v(13.53, 59.33) * mm, "end": v(13.53, 54.71) * mm});
            skLineSegment(sketch, "E68.7.1.0", {"start": v(18.15, 42.01) * mm, "end": v(13.53, 42.01) * mm});
            skLineSegment(sketch, "E68.7.1.1", {"start": v(18.15, 46.63) * mm, "end": v(18.15, 42.01) * mm});
            skLineSegment(sketch, "E68.7.1.2", {"start": v(18.15, 46.63) * mm, "end": v(13.53, 46.63) * mm});
            skLineSegment(sketch, "E68.7.1.3", {"start": v(13.53, 46.63) * mm, "end": v(13.53, 42.01) * mm});
            skLineSegment(sketch, "E68.7.2.0", {"start": v(18.15, 29.31) * mm, "end": v(13.53, 29.31) * mm});
            skLineSegment(sketch, "E68.7.2.1", {"start": v(18.15, 33.93) * mm, "end": v(18.15, 29.31) * mm});
            skLineSegment(sketch, "E68.7.2.2", {"start": v(18.15, 33.93) * mm, "end": v(13.53, 33.93) * mm});
            skLineSegment(sketch, "E68.7.2.3", {"start": v(13.53, 33.93) * mm, "end": v(13.53, 29.31) * mm});
            skLineSegment(sketch, "E68.7.3.0", {"start": v(18.15, 16.61) * mm, "end": v(13.53, 16.61) * mm});
            skLineSegment(sketch, "E68.7.3.1", {"start": v(18.15, 21.23) * mm, "end": v(18.15, 16.61) * mm});
            skLineSegment(sketch, "E68.7.3.2", {"start": v(18.15, 21.23) * mm, "end": v(13.53, 21.23) * mm});
            skLineSegment(sketch, "E68.7.3.3", {"start": v(13.53, 21.23) * mm, "end": v(13.53, 16.61) * mm});
            skLineSegment(sketch, "E68.7.4.0", {"start": v(18.15, 3.91) * mm, "end": v(13.53, 3.91) * mm});
            skLineSegment(sketch, "E68.7.4.1", {"start": v(18.15, 8.53) * mm, "end": v(18.15, 3.91) * mm});
            skLineSegment(sketch, "E68.7.4.2", {"start": v(18.15, 8.53) * mm, "end": v(13.53, 8.53) * mm});
            skLineSegment(sketch, "E68.7.4.3", {"start": v(13.53, 8.53) * mm, "end": v(13.53, 3.91) * mm});
            skLineSegment(sketch, "E68.8.0.0", {"start": v(5.45, 54.71) * mm, "end": v(0.83, 54.71) * mm});
            skLineSegment(sketch, "E68.8.0.1", {"start": v(5.45, 59.33) * mm, "end": v(5.45, 54.71) * mm});
            skLineSegment(sketch, "E68.8.0.2", {"start": v(5.45, 59.33) * mm, "end": v(0.83, 59.33) * mm});
            skLineSegment(sketch, "E68.8.0.3", {"start": v(0.83, 59.33) * mm, "end": v(0.83, 54.71) * mm});
            skLineSegment(sketch, "E68.8.1.0", {"start": v(5.45, 42.01) * mm, "end": v(0.83, 42.01) * mm});
            skLineSegment(sketch, "E68.8.1.1", {"start": v(5.45, 46.63) * mm, "end": v(5.45, 42.01) * mm});
            skLineSegment(sketch, "E68.8.1.2", {"start": v(5.45, 46.63) * mm, "end": v(0.83, 46.63) * mm});
            skLineSegment(sketch, "E68.8.1.3", {"start": v(0.83, 46.63) * mm, "end": v(0.83, 42.01) * mm});
            skLineSegment(sketch, "E68.8.2.0", {"start": v(5.45, 29.31) * mm, "end": v(0.83, 29.31) * mm});
            skLineSegment(sketch, "E68.8.2.1", {"start": v(5.45, 33.93) * mm, "end": v(5.45, 29.31) * mm});
            skLineSegment(sketch, "E68.8.2.2", {"start": v(5.45, 33.93) * mm, "end": v(0.83, 33.93) * mm});
            skLineSegment(sketch, "E68.8.2.3", {"start": v(0.83, 33.93) * mm, "end": v(0.83, 29.31) * mm});
            skLineSegment(sketch, "E68.8.3.0", {"start": v(5.45, 16.61) * mm, "end": v(0.83, 16.61) * mm});
            skLineSegment(sketch, "E68.8.3.1", {"start": v(5.45, 21.23) * mm, "end": v(5.45, 16.61) * mm});
            skLineSegment(sketch, "E68.8.3.2", {"start": v(5.45, 21.23) * mm, "end": v(0.83, 21.23) * mm});
            skLineSegment(sketch, "E68.8.3.3", {"start": v(0.83, 21.23) * mm, "end": v(0.83, 16.61) * mm});
            skLineSegment(sketch, "E68.8.4.0", {"start": v(5.45, 3.91) * mm, "end": v(0.83, 3.91) * mm});
            skLineSegment(sketch, "E68.8.4.1", {"start": v(5.45, 8.53) * mm, "end": v(5.45, 3.91) * mm});
            skLineSegment(sketch, "E68.8.4.2", {"start": v(5.45, 8.53) * mm, "end": v(0.83, 8.53) * mm});
            skLineSegment(sketch, "E68.8.4.3", {"start": v(0.83, 8.53) * mm, "end": v(0.83, 3.91) * mm});
            skLineSegment(sketch, "E68.9.0.0", {"start": v(-7.25, 54.71) * mm, "end": v(-11.87, 54.71) * mm});
            skLineSegment(sketch, "E68.9.0.1", {"start": v(-7.25, 59.33) * mm, "end": v(-7.25, 54.71) * mm});
            skLineSegment(sketch, "E68.9.0.2", {"start": v(-7.25, 59.33) * mm, "end": v(-11.87, 59.33) * mm});
            skLineSegment(sketch, "E68.9.0.3", {"start": v(-11.87, 59.33) * mm, "end": v(-11.87, 54.71) * mm});
            skLineSegment(sketch, "E68.9.1.0", {"start": v(-7.25, 42.01) * mm, "end": v(-11.87, 42.01) * mm});
            skLineSegment(sketch, "E68.9.1.1", {"start": v(-7.25, 46.63) * mm, "end": v(-7.25, 42.01) * mm});
            skLineSegment(sketch, "E68.9.1.2", {"start": v(-7.25, 46.63) * mm, "end": v(-11.87, 46.63) * mm});
            skLineSegment(sketch, "E68.9.1.3", {"start": v(-11.87, 46.63) * mm, "end": v(-11.87, 42.01) * mm});
            skLineSegment(sketch, "E68.9.2.0", {"start": v(-7.25, 29.31) * mm, "end": v(-11.87, 29.31) * mm});
            skLineSegment(sketch, "E68.9.2.1", {"start": v(-7.25, 33.93) * mm, "end": v(-7.25, 29.31) * mm});
            skLineSegment(sketch, "E68.9.2.2", {"start": v(-7.25, 33.93) * mm, "end": v(-11.87, 33.93) * mm});
            skLineSegment(sketch, "E68.9.2.3", {"start": v(-11.87, 33.93) * mm, "end": v(-11.87, 29.31) * mm});
            skLineSegment(sketch, "E68.9.3.0", {"start": v(-7.25, 16.61) * mm, "end": v(-11.87, 16.61) * mm});
            skLineSegment(sketch, "E68.9.3.1", {"start": v(-7.25, 21.23) * mm, "end": v(-7.25, 16.61) * mm});
            skLineSegment(sketch, "E68.9.3.2", {"start": v(-7.25, 21.23) * mm, "end": v(-11.87, 21.23) * mm});
            skLineSegment(sketch, "E68.9.3.3", {"start": v(-11.87, 21.23) * mm, "end": v(-11.87, 16.61) * mm});
            skLineSegment(sketch, "E68.9.4.0", {"start": v(-7.25, 3.91) * mm, "end": v(-11.87, 3.91) * mm});
            skLineSegment(sketch, "E68.9.4.1", {"start": v(-7.25, 8.53) * mm, "end": v(-7.25, 3.91) * mm});
            skLineSegment(sketch, "E68.9.4.2", {"start": v(-7.25, 8.53) * mm, "end": v(-11.87, 8.53) * mm});
            skLineSegment(sketch, "E68.9.4.3", {"start": v(-11.87, 8.53) * mm, "end": v(-11.87, 3.91) * mm});
            skLineSegment(sketch, "E68.10.0.0", {"start": v(-19.95, 54.71) * mm, "end": v(-24.57, 54.71) * mm});
            skLineSegment(sketch, "E68.10.0.1", {"start": v(-19.95, 59.33) * mm, "end": v(-19.95, 54.71) * mm});
            skLineSegment(sketch, "E68.10.0.2", {"start": v(-19.95, 59.33) * mm, "end": v(-24.57, 59.33) * mm});
            skLineSegment(sketch, "E68.10.0.3", {"start": v(-24.57, 59.33) * mm, "end": v(-24.57, 54.71) * mm});
            skLineSegment(sketch, "E68.10.1.0", {"start": v(-19.95, 42.01) * mm, "end": v(-24.57, 42.01) * mm});
            skLineSegment(sketch, "E68.10.1.1", {"start": v(-19.95, 46.63) * mm, "end": v(-19.95, 42.01) * mm});
            skLineSegment(sketch, "E68.10.1.2", {"start": v(-19.95, 46.63) * mm, "end": v(-24.57, 46.63) * mm});
            skLineSegment(sketch, "E68.10.1.3", {"start": v(-24.57, 46.63) * mm, "end": v(-24.57, 42.01) * mm});
            skLineSegment(sketch, "E68.10.2.0", {"start": v(-19.95, 29.31) * mm, "end": v(-24.57, 29.31) * mm});
            skLineSegment(sketch, "E68.10.2.1", {"start": v(-19.95, 33.93) * mm, "end": v(-19.95, 29.31) * mm});
            skLineSegment(sketch, "E68.10.2.2", {"start": v(-19.95, 33.93) * mm, "end": v(-24.57, 33.93) * mm});
            skLineSegment(sketch, "E68.10.2.3", {"start": v(-24.57, 33.93) * mm, "end": v(-24.57, 29.31) * mm});
            skLineSegment(sketch, "E68.10.3.0", {"start": v(-19.95, 16.61) * mm, "end": v(-24.57, 16.61) * mm});
            skLineSegment(sketch, "E68.10.3.1", {"start": v(-19.95, 21.23) * mm, "end": v(-19.95, 16.61) * mm});
            skLineSegment(sketch, "E68.10.3.2", {"start": v(-19.95, 21.23) * mm, "end": v(-24.57, 21.23) * mm});
            skLineSegment(sketch, "E68.10.3.3", {"start": v(-24.57, 21.23) * mm, "end": v(-24.57, 16.61) * mm});
            skLineSegment(sketch, "E68.10.4.0", {"start": v(-19.95, 3.91) * mm, "end": v(-24.57, 3.91) * mm});
            skLineSegment(sketch, "E68.10.4.1", {"start": v(-19.95, 8.53) * mm, "end": v(-19.95, 3.91) * mm});
            skLineSegment(sketch, "E68.10.4.2", {"start": v(-19.95, 8.53) * mm, "end": v(-24.57, 8.53) * mm});
            skLineSegment(sketch, "E68.10.4.3", {"start": v(-24.57, 8.53) * mm, "end": v(-24.57, 3.91) * mm});
            skLineSegment(sketch, "E68.11.0.0", {"start": v(-32.65, 54.71) * mm, "end": v(-37.27, 54.71) * mm});
            skLineSegment(sketch, "E68.11.0.1", {"start": v(-32.65, 59.33) * mm, "end": v(-32.65, 54.71) * mm});
            skLineSegment(sketch, "E68.11.0.2", {"start": v(-32.65, 59.33) * mm, "end": v(-37.27, 59.33) * mm});
            skLineSegment(sketch, "E68.11.0.3", {"start": v(-37.27, 59.33) * mm, "end": v(-37.27, 54.71) * mm});
            skLineSegment(sketch, "E68.11.1.0", {"start": v(-32.65, 42.01) * mm, "end": v(-37.27, 42.01) * mm});
            skLineSegment(sketch, "E68.11.1.1", {"start": v(-32.65, 46.63) * mm, "end": v(-32.65, 42.01) * mm});
            skLineSegment(sketch, "E68.11.1.2", {"start": v(-32.65, 46.63) * mm, "end": v(-37.27, 46.63) * mm});
            skLineSegment(sketch, "E68.11.1.3", {"start": v(-37.27, 46.63) * mm, "end": v(-37.27, 42.01) * mm});
            skLineSegment(sketch, "E68.11.2.0", {"start": v(-32.65, 29.31) * mm, "end": v(-37.27, 29.31) * mm});
            skLineSegment(sketch, "E68.11.2.1", {"start": v(-32.65, 33.93) * mm, "end": v(-32.65, 29.31) * mm});
            skLineSegment(sketch, "E68.11.2.2", {"start": v(-32.65, 33.93) * mm, "end": v(-37.27, 33.93) * mm});
            skLineSegment(sketch, "E68.11.2.3", {"start": v(-37.27, 33.93) * mm, "end": v(-37.27, 29.31) * mm});
            skLineSegment(sketch, "E68.11.3.0", {"start": v(-32.65, 16.61) * mm, "end": v(-37.27, 16.61) * mm});
            skLineSegment(sketch, "E68.11.3.1", {"start": v(-32.65, 21.23) * mm, "end": v(-32.65, 16.61) * mm});
            skLineSegment(sketch, "E68.11.3.2", {"start": v(-32.65, 21.23) * mm, "end": v(-37.27, 21.23) * mm});
            skLineSegment(sketch, "E68.11.3.3", {"start": v(-37.27, 21.23) * mm, "end": v(-37.27, 16.61) * mm});
            skLineSegment(sketch, "E68.11.4.0", {"start": v(-32.65, 3.91) * mm, "end": v(-37.27, 3.91) * mm});
            skLineSegment(sketch, "E68.11.4.1", {"start": v(-32.65, 8.53) * mm, "end": v(-32.65, 3.91) * mm});
            skLineSegment(sketch, "E68.11.4.2", {"start": v(-32.65, 8.53) * mm, "end": v(-37.27, 8.53) * mm});
            skLineSegment(sketch, "E68.11.4.3", {"start": v(-37.27, 8.53) * mm, "end": v(-37.27, 3.91) * mm});
            skLineSegment(sketch, "E68.12.0.0", {"start": v(-45.35, 54.71) * mm, "end": v(-49.97, 54.71) * mm});
            skLineSegment(sketch, "E68.12.0.1", {"start": v(-45.35, 59.33) * mm, "end": v(-45.35, 54.71) * mm});
            skLineSegment(sketch, "E68.12.0.2", {"start": v(-45.35, 59.33) * mm, "end": v(-49.97, 59.33) * mm});
            skLineSegment(sketch, "E68.12.0.3", {"start": v(-49.97, 59.33) * mm, "end": v(-49.97, 54.71) * mm});
            skLineSegment(sketch, "E68.12.1.0", {"start": v(-45.35, 42.01) * mm, "end": v(-49.97, 42.01) * mm});
            skLineSegment(sketch, "E68.12.1.1", {"start": v(-45.35, 46.63) * mm, "end": v(-45.35, 42.01) * mm});
            skLineSegment(sketch, "E68.12.1.2", {"start": v(-45.35, 46.63) * mm, "end": v(-49.97, 46.63) * mm});
            skLineSegment(sketch, "E68.12.1.3", {"start": v(-49.97, 46.63) * mm, "end": v(-49.97, 42.01) * mm});
            skLineSegment(sketch, "E68.12.2.0", {"start": v(-45.35, 29.31) * mm, "end": v(-49.97, 29.31) * mm});
            skLineSegment(sketch, "E68.12.2.1", {"start": v(-45.35, 33.93) * mm, "end": v(-45.35, 29.31) * mm});
            skLineSegment(sketch, "E68.12.2.2", {"start": v(-45.35, 33.93) * mm, "end": v(-49.97, 33.93) * mm});
            skLineSegment(sketch, "E68.12.2.3", {"start": v(-49.97, 33.93) * mm, "end": v(-49.97, 29.31) * mm});
            skLineSegment(sketch, "E68.12.3.0", {"start": v(-45.35, 16.61) * mm, "end": v(-49.97, 16.61) * mm});
            skLineSegment(sketch, "E68.12.3.1", {"start": v(-45.35, 21.23) * mm, "end": v(-45.35, 16.61) * mm});
            skLineSegment(sketch, "E68.12.3.2", {"start": v(-45.35, 21.23) * mm, "end": v(-49.97, 21.23) * mm});
            skLineSegment(sketch, "E68.12.3.3", {"start": v(-49.97, 21.23) * mm, "end": v(-49.97, 16.61) * mm});
            skLineSegment(sketch, "E68.12.4.0", {"start": v(-45.35, 3.91) * mm, "end": v(-49.97, 3.91) * mm});
            skLineSegment(sketch, "E68.12.4.1", {"start": v(-45.35, 8.53) * mm, "end": v(-45.35, 3.91) * mm});
            skLineSegment(sketch, "E68.12.4.2", {"start": v(-45.35, 8.53) * mm, "end": v(-49.97, 8.53) * mm});
            skLineSegment(sketch, "E68.12.4.3", {"start": v(-49.97, 8.53) * mm, "end": v(-49.97, 3.91) * mm});
            skLineSegment(sketch, "E68.13.0.0", {"start": v(-58.05, 54.71) * mm, "end": v(-62.67, 54.71) * mm});
            skLineSegment(sketch, "E68.13.0.1", {"start": v(-58.05, 59.33) * mm, "end": v(-58.05, 54.71) * mm});
            skLineSegment(sketch, "E68.13.0.2", {"start": v(-58.05, 59.33) * mm, "end": v(-62.67, 59.33) * mm});
            skLineSegment(sketch, "E68.13.0.3", {"start": v(-62.67, 59.33) * mm, "end": v(-62.67, 54.71) * mm});
            skLineSegment(sketch, "E68.13.1.0", {"start": v(-58.05, 42.01) * mm, "end": v(-62.67, 42.01) * mm});
            skLineSegment(sketch, "E68.13.1.1", {"start": v(-58.05, 46.63) * mm, "end": v(-58.05, 42.01) * mm});
            skLineSegment(sketch, "E68.13.1.2", {"start": v(-58.05, 46.63) * mm, "end": v(-62.67, 46.63) * mm});
            skLineSegment(sketch, "E68.13.1.3", {"start": v(-62.67, 46.63) * mm, "end": v(-62.67, 42.01) * mm});
            skLineSegment(sketch, "E68.13.2.0", {"start": v(-58.05, 29.31) * mm, "end": v(-62.67, 29.31) * mm});
            skLineSegment(sketch, "E68.13.2.1", {"start": v(-58.05, 33.93) * mm, "end": v(-58.05, 29.31) * mm});
            skLineSegment(sketch, "E68.13.2.2", {"start": v(-58.05, 33.93) * mm, "end": v(-62.67, 33.93) * mm});
            skLineSegment(sketch, "E68.13.2.3", {"start": v(-62.67, 33.93) * mm, "end": v(-62.67, 29.31) * mm});
            skLineSegment(sketch, "E68.13.3.0", {"start": v(-58.05, 16.61) * mm, "end": v(-62.67, 16.61) * mm});
            skLineSegment(sketch, "E68.13.3.1", {"start": v(-58.05, 21.23) * mm, "end": v(-58.05, 16.61) * mm});
            skLineSegment(sketch, "E68.13.3.2", {"start": v(-58.05, 21.23) * mm, "end": v(-62.67, 21.23) * mm});
            skLineSegment(sketch, "E68.13.3.3", {"start": v(-62.67, 21.23) * mm, "end": v(-62.67, 16.61) * mm});
            skLineSegment(sketch, "E68.13.4.0", {"start": v(-58.05, 3.91) * mm, "end": v(-62.67, 3.91) * mm});
            skLineSegment(sketch, "E68.13.4.1", {"start": v(-58.05, 8.53) * mm, "end": v(-58.05, 3.91) * mm});
            skLineSegment(sketch, "E68.13.4.2", {"start": v(-58.05, 8.53) * mm, "end": v(-62.67, 8.53) * mm});
            skLineSegment(sketch, "E68.13.4.3", {"start": v(-62.67, 8.53) * mm, "end": v(-62.67, 3.91) * mm});
            skLineSegment(sketch, "E68.direction1", {"start": v(102.43, 54.71) * mm, "end": v(89.73, 54.71) * mm, "construction": true});
            skLineSegment(sketch, "E68.direction2", {"start": v(102.43, 54.71) * mm, "end": v(102.43, 42.01) * mm, "construction": true});
            skLineSegment(sketch, "E69.0.14.0", {"start": v(-70.75, 54.71) * mm, "end": v(-75.37, 54.71) * mm});
            skLineSegment(sketch, "E69.3.14.0", {"start": v(-70.75, 59.33) * mm, "end": v(-70.75, 54.71) * mm});
            skLineSegment(sketch, "E69.6.14.0", {"start": v(-70.75, 59.33) * mm, "end": v(-75.37, 59.33) * mm});
            skLineSegment(sketch, "E69.9.14.0", {"start": v(-75.37, 59.33) * mm, "end": v(-75.37, 54.71) * mm});
            skLineSegment(sketch, "E69.0.14.1", {"start": v(-70.75, 42.01) * mm, "end": v(-75.37, 42.01) * mm});
            skLineSegment(sketch, "E69.3.14.1", {"start": v(-70.75, 46.63) * mm, "end": v(-70.75, 42.01) * mm});
            skLineSegment(sketch, "E69.6.14.1", {"start": v(-70.75, 46.63) * mm, "end": v(-75.37, 46.63) * mm});
            skLineSegment(sketch, "E69.9.14.1", {"start": v(-75.37, 46.63) * mm, "end": v(-75.37, 42.01) * mm});
            skLineSegment(sketch, "E69.0.14.2", {"start": v(-70.75, 29.31) * mm, "end": v(-75.37, 29.31) * mm});
            skLineSegment(sketch, "E69.3.14.2", {"start": v(-70.75, 33.93) * mm, "end": v(-70.75, 29.31) * mm});
            skLineSegment(sketch, "E69.6.14.2", {"start": v(-70.75, 33.93) * mm, "end": v(-75.37, 33.93) * mm});
            skLineSegment(sketch, "E69.9.14.2", {"start": v(-75.37, 33.93) * mm, "end": v(-75.37, 29.31) * mm});
            skLineSegment(sketch, "E69.0.14.3", {"start": v(-70.75, 16.61) * mm, "end": v(-75.37, 16.61) * mm});
            skLineSegment(sketch, "E69.3.14.3", {"start": v(-70.75, 21.23) * mm, "end": v(-70.75, 16.61) * mm});
            skLineSegment(sketch, "E69.6.14.3", {"start": v(-70.75, 21.23) * mm, "end": v(-75.37, 21.23) * mm});
            skLineSegment(sketch, "E69.9.14.3", {"start": v(-75.37, 21.23) * mm, "end": v(-75.37, 16.61) * mm});
            skLineSegment(sketch, "E69.0.14.4", {"start": v(-70.75, 3.91) * mm, "end": v(-75.37, 3.91) * mm});
            skLineSegment(sketch, "E69.3.14.4", {"start": v(-70.75, 8.53) * mm, "end": v(-70.75, 3.91) * mm});
            skLineSegment(sketch, "E69.6.14.4", {"start": v(-70.75, 8.53) * mm, "end": v(-75.37, 8.53) * mm});
            skLineSegment(sketch, "E69.9.14.4", {"start": v(-75.37, 8.53) * mm, "end": v(-75.37, 3.91) * mm});
            skLineSegment(sketch, "E69.0.15.0", {"start": v(-83.45, 54.71) * mm, "end": v(-88.07, 54.71) * mm});
            skLineSegment(sketch, "E69.3.15.0", {"start": v(-83.45, 59.33) * mm, "end": v(-83.45, 54.71) * mm});
            skLineSegment(sketch, "E69.6.15.0", {"start": v(-83.45, 59.33) * mm, "end": v(-88.07, 59.33) * mm});
            skLineSegment(sketch, "E69.9.15.0", {"start": v(-88.07, 59.33) * mm, "end": v(-88.07, 54.71) * mm});
            skLineSegment(sketch, "E69.0.15.1", {"start": v(-83.45, 42.01) * mm, "end": v(-88.07, 42.01) * mm});
            skLineSegment(sketch, "E69.3.15.1", {"start": v(-83.45, 46.63) * mm, "end": v(-83.45, 42.01) * mm});
            skLineSegment(sketch, "E69.6.15.1", {"start": v(-83.45, 46.63) * mm, "end": v(-88.07, 46.63) * mm});
            skLineSegment(sketch, "E69.9.15.1", {"start": v(-88.07, 46.63) * mm, "end": v(-88.07, 42.01) * mm});
            skLineSegment(sketch, "E69.0.15.2", {"start": v(-83.45, 29.31) * mm, "end": v(-88.07, 29.31) * mm});
            skLineSegment(sketch, "E69.3.15.2", {"start": v(-83.45, 33.93) * mm, "end": v(-83.45, 29.31) * mm});
            skLineSegment(sketch, "E69.6.15.2", {"start": v(-83.45, 33.93) * mm, "end": v(-88.07, 33.93) * mm});
            skLineSegment(sketch, "E69.9.15.2", {"start": v(-88.07, 33.93) * mm, "end": v(-88.07, 29.31) * mm});
            skLineSegment(sketch, "E69.0.15.3", {"start": v(-83.45, 16.61) * mm, "end": v(-88.07, 16.61) * mm});
            skLineSegment(sketch, "E69.3.15.3", {"start": v(-83.45, 21.23) * mm, "end": v(-83.45, 16.61) * mm});
            skLineSegment(sketch, "E69.6.15.3", {"start": v(-83.45, 21.23) * mm, "end": v(-88.07, 21.23) * mm});
            skLineSegment(sketch, "E69.9.15.3", {"start": v(-88.07, 21.23) * mm, "end": v(-88.07, 16.61) * mm});
            skLineSegment(sketch, "E69.0.15.4", {"start": v(-83.45, 3.91) * mm, "end": v(-88.07, 3.91) * mm});
            skLineSegment(sketch, "E69.3.15.4", {"start": v(-83.45, 8.53) * mm, "end": v(-83.45, 3.91) * mm});
            skLineSegment(sketch, "E69.6.15.4", {"start": v(-83.45, 8.53) * mm, "end": v(-88.07, 8.53) * mm});
            skLineSegment(sketch, "E69.9.15.4", {"start": v(-88.07, 8.53) * mm, "end": v(-88.07, 3.91) * mm});
            skSolve(sketch);
        }
        {
            var Q0;
            Q0=makeQuery(id+"F1.imprint","IMPRINT",FACE,{"disambiguationData":[TD([[makeQuery(id+"F1.imprint","IMPRINT",EDGE,{"derivedFrom":sQuery(id+"F1.wireOp",EDGE,"E63")}),1.0]])]});
            var Q1;
            {var subQ1=sQuery(id+"F1.wireOp",EDGE,"8ea1a07a-7ca9-4907-9e18-5108a9660366");Q1=makeQuery(id+"F1.imprint","IMPRINT",FACE,{"disambiguationData":[TD([[makeQuery(id+"F1.imprint","IMPRINT",EDGE,{"derivedFrom":subQ1}),1.0]])]});}
            extrude(context, id + "F2", {"entities" : qUnion([Q0, Q1]), "depth" : 2.54 * mm});
        }
        {
            var Q0;
            Q0=makeQuery(id+"F0.imprint","IMPRINT",FACE,{"disambiguationData":[TD([[makeQuery(id+"F0.imprint","IMPRINT",EDGE,{"derivedFrom":sQuery(id+"F0.wireOp",EDGE,"E0.bottom")}),-1.0]])]});
            extrude(context, id + "F3", {"entities" : qUnion([Q0]), "oppositeDirection" : true, "depth" : 2.54 * mm});
        }
    });
